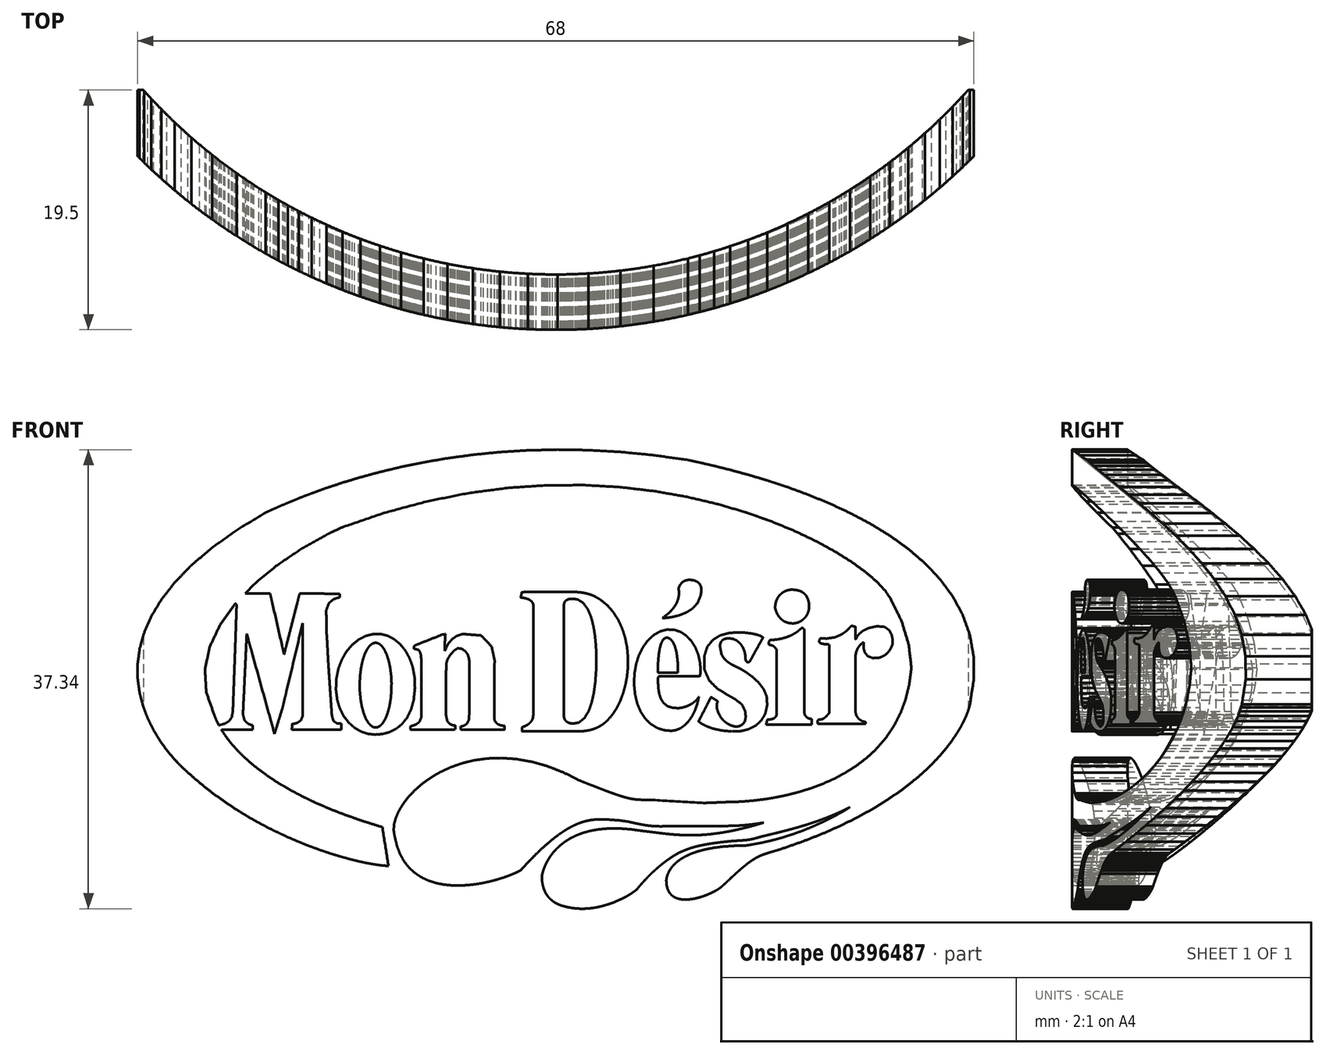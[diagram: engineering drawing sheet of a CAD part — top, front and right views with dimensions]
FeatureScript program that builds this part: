
annotation { "Feature Type Name" : "Feature", "Feature Type Description" : "" }
export const myFeature = defineFeature(function(context is Context, id is Id, definition is map)
    precondition{}
    {
        {
            var Q0;
            Q0=qCreatedBy(makeId("Front.planeOp"),FACE);
            var sketch = newSketch(context, id + "F0", { "sketchPlane" : qUnion([Q0])});
            skLineSegment(sketch, "E0", {"start": v(-8.17, -3.89) * mm, "end": v(-8.17, -4) * mm});
            skLineSegment(sketch, "E1", {"start": v(-7.14, 1.98) * mm, "end": v(-7.35, 2.28) * mm});
            skLineSegment(sketch, "E2", {"start": v(-7.35, 2.28) * mm, "end": v(-7.63, 2.47) * mm});
            skLineSegment(sketch, "E3", {"start": v(-5.22, 2.66) * mm, "end": v(-4.97, 1.53) * mm});
            skLineSegment(sketch, "E4", {"start": v(-6.04, -4.1) * mm, "end": v(-7.2, -4.1) * mm});
            skLineSegment(sketch, "E5", {"start": v(-7.56, 3.68) * mm, "end": v(-6.07, 3.56) * mm});
            skLineSegment(sketch, "E6", {"start": v(-7.63, 2.47) * mm, "end": v(-7.95, 2.52) * mm});
            skLineSegment(sketch, "E7", {"start": v(-8.24, 2.35) * mm, "end": v(-8.55, 2.01) * mm});
            skLineSegment(sketch, "E8", {"start": v(-8.55, 2.01) * mm, "end": v(-8.8, 1.6) * mm});
            skLineSegment(sketch, "E9", {"start": v(-7.95, 2.52) * mm, "end": v(-8.24, 2.35) * mm});
            skLineSegment(sketch, "E10", {"start": v(-8.91, 0.7) * mm, "end": v(-8.92, -0.57) * mm});
            skLineSegment(sketch, "E11", {"start": v(-7.04, 1.63) * mm, "end": v(-7.14, 1.98) * mm});
            skLineSegment(sketch, "E12", {"start": v(-8.93, -2) * mm, "end": v(-8.9, -3.03) * mm});
            skLineSegment(sketch, "E13", {"start": v(-6.07, 3.56) * mm, "end": v(-5.22, 2.66) * mm});
            skLineSegment(sketch, "E14", {"start": v(-4.16, -3.8) * mm, "end": v(-4.16, -3.87) * mm});
            skLineSegment(sketch, "E15", {"start": v(-4.22, -3.8) * mm, "end": v(-4.16, -3.8) * mm});
            skLineSegment(sketch, "E16", {"start": v(-4.16, -4.07) * mm, "end": v(-4.17, -4.1) * mm});
            skLineSegment(sketch, "E17", {"start": v(-7.21, -3.61) * mm, "end": v(-7.05, -3.28) * mm});
            skLineSegment(sketch, "E18", {"start": v(-7.05, -3.28) * mm, "end": v(-7.03, -2.64) * mm});
            skLineSegment(sketch, "E19", {"start": v(-7.03, 1.16) * mm, "end": v(-7.03, 1.43) * mm});
            skLineSegment(sketch, "E20", {"start": v(-4.16, -3.97) * mm, "end": v(-4.16, -4.07) * mm});
            skLineSegment(sketch, "E21", {"start": v(-9.01, 2.3) * mm, "end": v(-8.77, 2.86) * mm});
            skLineSegment(sketch, "E22", {"start": v(-7.03, 0.56) * mm, "end": v(-7.03, 0.81) * mm});
            skLineSegment(sketch, "E23", {"start": v(-7.73, -3.98) * mm, "end": v(-7.74, -3.9) * mm});
            skLineSegment(sketch, "E24", {"start": v(-8.9, -3.03) * mm, "end": v(-8.8, -3.45) * mm});
            skLineSegment(sketch, "E25", {"start": v(-8.8, -3.45) * mm, "end": v(-8.58, -3.67) * mm});
            skLineSegment(sketch, "E26", {"start": v(-4.16, -3.87) * mm, "end": v(-4.16, -3.97) * mm});
            skLineSegment(sketch, "E27", {"start": v(-4.99, -2.85) * mm, "end": v(-4.97, -3.37) * mm});
            skLineSegment(sketch, "E28", {"start": v(-8.58, -3.67) * mm, "end": v(-8.33, -3.75) * mm});
            skLineSegment(sketch, "E29", {"start": v(-8.33, -3.75) * mm, "end": v(-8.18, -3.77) * mm});
            skLineSegment(sketch, "E30", {"start": v(-8.18, -3.77) * mm, "end": v(-8.17, -3.8) * mm});
            skLineSegment(sketch, "E31", {"start": v(-4.76, -3.63) * mm, "end": v(-4.46, -3.76) * mm});
            skLineSegment(sketch, "E32", {"start": v(-8.17, -3.8) * mm, "end": v(-8.17, -3.89) * mm});
            skLineSegment(sketch, "E33", {"start": v(-8.92, -0.57) * mm, "end": v(-8.93, -2) * mm});
            skLineSegment(sketch, "E34", {"start": v(-4.98, -1.75) * mm, "end": v(-4.99, -2.85) * mm});
            skLineSegment(sketch, "E35", {"start": v(-7.46, -3.78) * mm, "end": v(-7.21, -3.61) * mm});
            skLineSegment(sketch, "E36", {"start": v(-8.02, 3.53) * mm, "end": v(-7.56, 3.68) * mm});
            skLineSegment(sketch, "E37", {"start": v(-7.2, -4.1) * mm, "end": v(-7.72, -4.1) * mm});
            skLineSegment(sketch, "E38", {"start": v(-7.72, -4.06) * mm, "end": v(-7.73, -3.98) * mm});
            skLineSegment(sketch, "E39", {"start": v(-7.74, -3.85) * mm, "end": v(-7.67, -3.84) * mm});
            skLineSegment(sketch, "E40", {"start": v(-4.99, -0.48) * mm, "end": v(-4.98, -1.75) * mm});
            skLineSegment(sketch, "E41", {"start": v(-17.58, 6.79) * mm, "end": v(-17.58, 6.69) * mm});
            skLineSegment(sketch, "E42", {"start": v(-8.43, 3.26) * mm, "end": v(-8.02, 3.53) * mm});
            skLineSegment(sketch, "E43", {"start": v(-7.03, -2.64) * mm, "end": v(-7.02, -1.53) * mm});
            skLineSegment(sketch, "E44", {"start": v(-7.03, 0.81) * mm, "end": v(-7.03, 1.16) * mm});
            skLineSegment(sketch, "E45", {"start": v(-7.03, 1.43) * mm, "end": v(-7.04, 1.63) * mm});
            skLineSegment(sketch, "E46", {"start": v(-7.74, -3.9) * mm, "end": v(-7.74, -3.85) * mm});
            skLineSegment(sketch, "E47", {"start": v(-8.8, 1.6) * mm, "end": v(-8.9, 1.25) * mm});
            skLineSegment(sketch, "E48", {"start": v(-7.67, -3.84) * mm, "end": v(-7.46, -3.78) * mm});
            skLineSegment(sketch, "E49", {"start": v(-4.17, -4.1) * mm, "end": v(-4.84, -4.1) * mm});
            skLineSegment(sketch, "E50", {"start": v(-4.46, -3.76) * mm, "end": v(-4.22, -3.8) * mm});
            skLineSegment(sketch, "E51", {"start": v(-4.84, -4.1) * mm, "end": v(-6.04, -4.1) * mm});
            skLineSegment(sketch, "E52", {"start": v(-5, 0.49) * mm, "end": v(-4.99, -0.48) * mm});
            skLineSegment(sketch, "E53", {"start": v(-8.77, 2.86) * mm, "end": v(-8.43, 3.26) * mm});
            skLineSegment(sketch, "E54", {"start": v(-7.72, -4.1) * mm, "end": v(-7.72, -4.06) * mm});
            skLineSegment(sketch, "E55", {"start": v(-7.03, 0.4) * mm, "end": v(-7.03, 0.56) * mm});
            skLineSegment(sketch, "E56", {"start": v(-8.9, 1.25) * mm, "end": v(-8.91, 0.7) * mm});
            skLineSegment(sketch, "E57", {"start": v(-17.58, 6.69) * mm, "end": v(-17.58, 6.64) * mm});
            skLineSegment(sketch, "E58", {"start": v(-4.99, 0.78) * mm, "end": v(-5, 0.49) * mm});
            skLineSegment(sketch, "E59", {"start": v(-4.97, -3.37) * mm, "end": v(-4.76, -3.63) * mm});
            skLineSegment(sketch, "E60", {"start": v(-4.97, 1.53) * mm, "end": v(-4.99, 0.78) * mm});
            skLineSegment(sketch, "E61", {"start": v(-7.02, -1.53) * mm, "end": v(-7.03, -0.38) * mm});
            skLineSegment(sketch, "E62", {"start": v(-7.03, -0.38) * mm, "end": v(-7.03, 0.4) * mm});
            skLineSegment(sketch, "E63", {"start": v(-17.42, -3.85) * mm, "end": v(-17.42, -4.02) * mm});
            skLineSegment(sketch, "E64", {"start": v(-17.42, -4.02) * mm, "end": v(-17.42, -4.1) * mm});
            skLineSegment(sketch, "E65", {"start": v(-18.3, -1.5) * mm, "end": v(-18.2, -2.99) * mm});
            skLineSegment(sketch, "E66", {"start": v(-17.42, -4.1) * mm, "end": v(-18.05, -4.1) * mm});
            skLineSegment(sketch, "E67", {"start": v(-18.05, -4.1) * mm, "end": v(-19.44, -4.1) * mm});
            skLineSegment(sketch, "E68", {"start": v(-18.64, 3.93) * mm, "end": v(-18.49, 1.18) * mm});
            skLineSegment(sketch, "E69", {"start": v(-19.44, -4.1) * mm, "end": v(-20.83, -4.1) * mm});
            skLineSegment(sketch, "E70", {"start": v(-21.43, -3.65) * mm, "end": v(-21.3, -3.63) * mm});
            skLineSegment(sketch, "E71", {"start": v(-20.83, -4.1) * mm, "end": v(-21.46, -4.1) * mm});
            skLineSegment(sketch, "E72", {"start": v(-17.73, 6.62) * mm, "end": v(-18.08, 6.5) * mm});
            skLineSegment(sketch, "E73", {"start": v(-18.49, 1.18) * mm, "end": v(-18.3, -1.5) * mm});
            skLineSegment(sketch, "E74", {"start": v(-17.58, 6.64) * mm, "end": v(-17.73, 6.62) * mm});
            skLineSegment(sketch, "E75", {"start": v(-17.54, -3.61) * mm, "end": v(-17.42, -3.6) * mm});
            skLineSegment(sketch, "E76", {"start": v(-17.42, -3.68) * mm, "end": v(-17.42, -3.85) * mm});
            skLineSegment(sketch, "E77", {"start": v(-21.46, -4.1) * mm, "end": v(-21.46, -4.03) * mm});
            skLineSegment(sketch, "E78", {"start": v(-21.46, -4.03) * mm, "end": v(-21.45, -3.87) * mm});
            skLineSegment(sketch, "E79", {"start": v(-21.44, -3.72) * mm, "end": v(-21.43, -3.65) * mm});
            skLineSegment(sketch, "E80", {"start": v(-21.3, -3.63) * mm, "end": v(-21.02, -3.55) * mm});
            skLineSegment(sketch, "E81", {"start": v(-18.66, 5.6) * mm, "end": v(-18.64, 3.93) * mm});
            skLineSegment(sketch, "E82", {"start": v(-21.02, -3.55) * mm, "end": v(-20.72, -3.35) * mm});
            skLineSegment(sketch, "E83", {"start": v(-18.2, -2.99) * mm, "end": v(-18.06, -3.41) * mm});
            skLineSegment(sketch, "E84", {"start": v(-18.45, 6.19) * mm, "end": v(-18.66, 5.6) * mm});
            skLineSegment(sketch, "E85", {"start": v(-17.42, -3.6) * mm, "end": v(-17.42, -3.68) * mm});
            skLineSegment(sketch, "E86", {"start": v(-20.72, -3.35) * mm, "end": v(-20.58, -2.99) * mm});
            skLineSegment(sketch, "E87", {"start": v(-21.45, -3.87) * mm, "end": v(-21.44, -3.72) * mm});
            skLineSegment(sketch, "E88", {"start": v(-18.06, -3.41) * mm, "end": v(-17.8, -3.59) * mm});
            skLineSegment(sketch, "E89", {"start": v(-20.58, -2.99) * mm, "end": v(-20.57, -1.55) * mm});
            skLineSegment(sketch, "E90", {"start": v(-18.08, 6.5) * mm, "end": v(-18.45, 6.19) * mm});
            skLineSegment(sketch, "E91", {"start": v(-17.8, -3.59) * mm, "end": v(-17.54, -3.61) * mm});
            skLineSegment(sketch, "E92", {"start": v(-27.4, -3.8) * mm, "end": v(-27.4, -3.75) * mm});
            skLineSegment(sketch, "E93", {"start": v(-26.97, -4.1) * mm, "end": v(-27.4, -4.1) * mm});
            skLineSegment(sketch, "E94", {"start": v(-21.96, -1.24) * mm, "end": v(-22.21, -2.31) * mm});
            skLineSegment(sketch, "E95", {"start": v(-22.77, -4.12) * mm, "end": v(-22.87, -4.45) * mm});
            skLineSegment(sketch, "E96", {"start": v(-25.18, 2.67) * mm, "end": v(-25.28, 0.41) * mm});
            skLineSegment(sketch, "E97", {"start": v(-27.4, -4.04) * mm, "end": v(-27.4, -3.93) * mm});
            skLineSegment(sketch, "E98", {"start": v(-24.78, 2.42) * mm, "end": v(-25.13, 3.7) * mm});
            skLineSegment(sketch, "E99", {"start": v(-26.82, 6.61) * mm, "end": v(-26.98, 6.64) * mm});
            skLineSegment(sketch, "E100", {"start": v(-26, 4.46) * mm, "end": v(-25.95, 6.01) * mm});
            skLineSegment(sketch, "E101", {"start": v(-22.27, 2.8) * mm, "end": v(-22.1, 2.01) * mm});
            skLineSegment(sketch, "E102", {"start": v(-23.05, 6.2) * mm, "end": v(-22.66, 4.5) * mm});
            skLineSegment(sketch, "E103", {"start": v(-21.02, 6.2) * mm, "end": v(-20.82, 6.99) * mm});
            skLineSegment(sketch, "E104", {"start": v(-20.82, 6.99) * mm, "end": v(-20.31, 6.98) * mm});
            skLineSegment(sketch, "E105", {"start": v(-21.4, 1.12) * mm, "end": v(-21.96, -1.24) * mm});
            skLineSegment(sketch, "E106", {"start": v(-27.4, -3.93) * mm, "end": v(-27.4, -3.8) * mm});
            skLineSegment(sketch, "E107", {"start": v(-26.98, 6.81) * mm, "end": v(-26.98, 6.93) * mm});
            skLineSegment(sketch, "E108", {"start": v(-26.34, -3.08) * mm, "end": v(-26.26, -2.63) * mm});
            skLineSegment(sketch, "E109", {"start": v(-26.98, 6.93) * mm, "end": v(-26.98, 6.99) * mm});
            skLineSegment(sketch, "E110", {"start": v(-25.13, 3.7) * mm, "end": v(-25.18, 2.67) * mm});
            skLineSegment(sketch, "E111", {"start": v(-26.46, 6.5) * mm, "end": v(-26.82, 6.61) * mm});
            skLineSegment(sketch, "E112", {"start": v(-26.98, 6.99) * mm, "end": v(-26.4, 6.99) * mm});
            skLineSegment(sketch, "E113", {"start": v(-20.83, 3.48) * mm, "end": v(-21.4, 1.12) * mm});
            skLineSegment(sketch, "E114", {"start": v(-26.4, 6.99) * mm, "end": v(-25.1, 6.99) * mm});
            skLineSegment(sketch, "E115", {"start": v(-24, -0.38) * mm, "end": v(-24.78, 2.42) * mm});
            skLineSegment(sketch, "E116", {"start": v(-24.77, -3.73) * mm, "end": v(-24.64, -3.75) * mm});
            skLineSegment(sketch, "E117", {"start": v(-22.54, -3.38) * mm, "end": v(-22.77, -4.12) * mm});
            skLineSegment(sketch, "E118", {"start": v(-26.11, 1.51) * mm, "end": v(-26, 4.46) * mm});
            skLineSegment(sketch, "E119", {"start": v(-20.58, 4.56) * mm, "end": v(-20.83, 3.48) * mm});
            skLineSegment(sketch, "E120", {"start": v(-25.31, -3.34) * mm, "end": v(-25.04, -3.6) * mm});
            skLineSegment(sketch, "E121", {"start": v(-26.55, -3.4) * mm, "end": v(-26.34, -3.08) * mm});
            skLineSegment(sketch, "E122", {"start": v(-26.98, 6.64) * mm, "end": v(-26.98, 6.7) * mm});
            skLineSegment(sketch, "E123", {"start": v(-25.07, -4.1) * mm, "end": v(-26.02, -4.1) * mm});
            skLineSegment(sketch, "E124", {"start": v(-26.98, 6.7) * mm, "end": v(-26.98, 6.81) * mm});
            skLineSegment(sketch, "E125", {"start": v(-27.4, -3.75) * mm, "end": v(-26.9, -3.61) * mm});
            skLineSegment(sketch, "E126", {"start": v(-27.4, -4.1) * mm, "end": v(-27.4, -4.04) * mm});
            skLineSegment(sketch, "E127", {"start": v(-25.28, 0.41) * mm, "end": v(-25.39, -1.84) * mm});
            skLineSegment(sketch, "E128", {"start": v(-22.21, -2.31) * mm, "end": v(-22.32, -2.65) * mm});
            skLineSegment(sketch, "E129", {"start": v(-24.64, -4.1) * mm, "end": v(-25.07, -4.1) * mm});
            skLineSegment(sketch, "E130", {"start": v(-23.82, 6.99) * mm, "end": v(-23.23, 6.99) * mm});
            skLineSegment(sketch, "E131", {"start": v(-23.23, 6.99) * mm, "end": v(-23.05, 6.2) * mm});
            skLineSegment(sketch, "E132", {"start": v(-26.21, -1.35) * mm, "end": v(-26.11, 1.51) * mm});
            skLineSegment(sketch, "E133", {"start": v(-25.04, -3.6) * mm, "end": v(-24.77, -3.73) * mm});
            skLineSegment(sketch, "E134", {"start": v(-20.57, 1.02) * mm, "end": v(-20.57, 3.47) * mm});
            skLineSegment(sketch, "E135", {"start": v(-20.57, -1.55) * mm, "end": v(-20.57, 1.02) * mm});
            skLineSegment(sketch, "E136", {"start": v(-20.57, 3.47) * mm, "end": v(-20.58, 4.56) * mm});
            skLineSegment(sketch, "E137", {"start": v(-22.32, -2.65) * mm, "end": v(-22.54, -3.38) * mm});
            skLineSegment(sketch, "E138", {"start": v(-25.44, -2.86) * mm, "end": v(-25.31, -3.34) * mm});
            skLineSegment(sketch, "E139", {"start": v(-26.02, -4.1) * mm, "end": v(-26.97, -4.1) * mm});
            skLineSegment(sketch, "E140", {"start": v(-26.9, -3.61) * mm, "end": v(-26.55, -3.4) * mm});
            skLineSegment(sketch, "E141", {"start": v(-23.22, -3.18) * mm, "end": v(-24, -0.38) * mm});
            skLineSegment(sketch, "E142", {"start": v(-25.95, 6.01) * mm, "end": v(-26.11, 6.31) * mm});
            skLineSegment(sketch, "E143", {"start": v(-26.11, 6.31) * mm, "end": v(-26.46, 6.5) * mm});
            skLineSegment(sketch, "E144", {"start": v(-26.26, -2.63) * mm, "end": v(-26.21, -1.35) * mm});
            skLineSegment(sketch, "E145", {"start": v(-22.87, -4.45) * mm, "end": v(-23.22, -3.18) * mm});
            skLineSegment(sketch, "E146", {"start": v(-25.39, -1.84) * mm, "end": v(-25.44, -2.86) * mm});
            skLineSegment(sketch, "E147", {"start": v(-22.66, 4.5) * mm, "end": v(-22.27, 2.8) * mm});
            skLineSegment(sketch, "E148", {"start": v(-22.1, 2.01) * mm, "end": v(-21.9, 2.8) * mm});
            skLineSegment(sketch, "E149", {"start": v(-21.9, 2.8) * mm, "end": v(-21.46, 4.5) * mm});
            skLineSegment(sketch, "E150", {"start": v(-25.1, 6.99) * mm, "end": v(-23.82, 6.99) * mm});
            skLineSegment(sketch, "E151", {"start": v(-21.46, 4.5) * mm, "end": v(-21.02, 6.2) * mm});
            skLineSegment(sketch, "E152", {"start": v(-17.58, 6.9) * mm, "end": v(-17.58, 6.79) * mm});
            skLineSegment(sketch, "E153", {"start": v(-20.31, 6.98) * mm, "end": v(-19.2, 6.96) * mm});
            skLineSegment(sketch, "E154", {"start": v(-19.2, 6.96) * mm, "end": v(-18.08, 6.94) * mm});
            skLineSegment(sketch, "E155", {"start": v(-18.08, 6.94) * mm, "end": v(-17.58, 6.94) * mm});
            skLineSegment(sketch, "E156", {"start": v(-17.58, 6.94) * mm, "end": v(-17.58, 6.9) * mm});
            skLineSegment(sketch, "E157", {"start": v(7.1, 2.62) * mm, "end": v(7.51, 3.17) * mm});
            skLineSegment(sketch, "E158", {"start": v(1.44, -3.62) * mm, "end": v(1.89, -3.52) * mm});
            skLineSegment(sketch, "E159", {"start": v(11.32, -2.57) * mm, "end": v(11.08, -3.04) * mm});
            skLineSegment(sketch, "E160", {"start": v(9.79, -4.14) * mm, "end": v(9.41, -4.2) * mm});
            skLineSegment(sketch, "E161", {"start": v(0.66, 2.96) * mm, "end": v(0.66, 1.33) * mm});
            skLineSegment(sketch, "E162", {"start": v(6.4, 0.45) * mm, "end": v(6.54, 1.25) * mm});
            skLineSegment(sketch, "E163", {"start": v(7.51, 3.17) * mm, "end": v(7.98, 3.6) * mm});
            skLineSegment(sketch, "E164", {"start": v(6.46, -1.26) * mm, "end": v(6.37, -0.41) * mm});
            skLineSegment(sketch, "E165", {"start": v(0.68, 6.18) * mm, "end": v(0.66, 6.01) * mm});
            skLineSegment(sketch, "E166", {"start": v(3.1, -1.07) * mm, "end": v(3.22, -0.22) * mm});
            skLineSegment(sketch, "E167", {"start": v(3.27, 2.77) * mm, "end": v(3.19, 3.56) * mm});
            skLineSegment(sketch, "E168", {"start": v(7.98, 3.6) * mm, "end": v(8.5, 3.9) * mm});
            skLineSegment(sketch, "E169", {"start": v(8.5, 3.9) * mm, "end": v(9.07, 4.04) * mm});
            skLineSegment(sketch, "E170", {"start": v(0.66, -1.68) * mm, "end": v(0.66, -2.67) * mm});
            skLineSegment(sketch, "E171", {"start": v(1.26, -3.6) * mm, "end": v(1.36, -3.61) * mm});
            skLineSegment(sketch, "E172", {"start": v(11.5, -2.03) * mm, "end": v(11.32, -2.57) * mm});
            skLineSegment(sketch, "E173", {"start": v(7.73, -3.65) * mm, "end": v(7.29, -3.22) * mm});
            skLineSegment(sketch, "E174", {"start": v(1.1, 6.52) * mm, "end": v(0.97, 6.48) * mm});
            skLineSegment(sketch, "E175", {"start": v(0.66, -2.67) * mm, "end": v(0.66, -3.04) * mm});
            skLineSegment(sketch, "E176", {"start": v(3.22, -0.22) * mm, "end": v(3.28, 0.61) * mm});
            skLineSegment(sketch, "E177", {"start": v(3.3, 2.03) * mm, "end": v(3.27, 2.77) * mm});
            skLineSegment(sketch, "E178", {"start": v(0.7, -3.22) * mm, "end": v(0.79, -3.36) * mm});
            skLineSegment(sketch, "E179", {"start": v(1.02, -3.53) * mm, "end": v(1.14, -3.57) * mm});
            skLineSegment(sketch, "E180", {"start": v(3.06, 4.35) * mm, "end": v(2.86, 5.09) * mm});
            skLineSegment(sketch, "E181", {"start": v(1.77, 6.49) * mm, "end": v(1.42, 6.54) * mm});
            skLineSegment(sketch, "E182", {"start": v(1.34, 6.54) * mm, "end": v(1.23, 6.54) * mm});
            skLineSegment(sketch, "E183", {"start": v(0.66, 4.42) * mm, "end": v(0.66, 2.96) * mm});
            skLineSegment(sketch, "E184", {"start": v(0.66, -0.29) * mm, "end": v(0.66, -1.68) * mm});
            skLineSegment(sketch, "E185", {"start": v(10.8, -3.43) * mm, "end": v(10.49, -3.75) * mm});
            skLineSegment(sketch, "E186", {"start": v(8.82, -4.15) * mm, "end": v(8.25, -3.97) * mm});
            skLineSegment(sketch, "E187", {"start": v(1.89, -3.52) * mm, "end": v(2.33, -3.17) * mm});
            skLineSegment(sketch, "E188", {"start": v(7.29, -3.22) * mm, "end": v(6.92, -2.67) * mm});
            skLineSegment(sketch, "E189", {"start": v(6.92, -2.67) * mm, "end": v(6.64, -2.02) * mm});
            skLineSegment(sketch, "E190", {"start": v(3.19, 3.56) * mm, "end": v(3.06, 4.35) * mm});
            skLineSegment(sketch, "E191", {"start": v(0.79, -3.36) * mm, "end": v(0.9, -3.46) * mm});
            skLineSegment(sketch, "E192", {"start": v(0.97, 6.48) * mm, "end": v(0.85, 6.42) * mm});
            skLineSegment(sketch, "E193", {"start": v(0.9, -3.46) * mm, "end": v(1.02, -3.53) * mm});
            skLineSegment(sketch, "E194", {"start": v(3.3, 1.37) * mm, "end": v(3.3, 2.03) * mm});
            skLineSegment(sketch, "E195", {"start": v(0.85, 6.42) * mm, "end": v(0.75, 6.32) * mm});
            skLineSegment(sketch, "E196", {"start": v(0.66, 1.33) * mm, "end": v(0.66, -0.29) * mm});
            skLineSegment(sketch, "E197", {"start": v(1.14, -3.57) * mm, "end": v(1.26, -3.6) * mm});
            skLineSegment(sketch, "E198", {"start": v(2.23, 6.2) * mm, "end": v(1.77, 6.49) * mm});
            skLineSegment(sketch, "E199", {"start": v(11.64, -1.44) * mm, "end": v(11.5, -2.03) * mm});
            skLineSegment(sketch, "E200", {"start": v(9.41, -4.2) * mm, "end": v(8.82, -4.15) * mm});
            skLineSegment(sketch, "E201", {"start": v(8.25, -3.97) * mm, "end": v(7.73, -3.65) * mm});
            skLineSegment(sketch, "E202", {"start": v(10.49, -3.75) * mm, "end": v(10.15, -4) * mm});
            skLineSegment(sketch, "E203", {"start": v(1.23, 6.54) * mm, "end": v(1.1, 6.52) * mm});
            skLineSegment(sketch, "E204", {"start": v(10.15, -4) * mm, "end": v(9.79, -4.14) * mm});
            skLineSegment(sketch, "E205", {"start": v(0.66, 6.01) * mm, "end": v(0.66, 5.5) * mm});
            skLineSegment(sketch, "E206", {"start": v(2.6, 5.73) * mm, "end": v(2.23, 6.2) * mm});
            skLineSegment(sketch, "E207", {"start": v(1.36, -3.61) * mm, "end": v(1.44, -3.62) * mm});
            skLineSegment(sketch, "E208", {"start": v(6.64, -2.02) * mm, "end": v(6.46, -1.26) * mm});
            skLineSegment(sketch, "E209", {"start": v(2.33, -3.17) * mm, "end": v(2.68, -2.6) * mm});
            skLineSegment(sketch, "E210", {"start": v(1.42, 6.54) * mm, "end": v(1.34, 6.54) * mm});
            skLineSegment(sketch, "E211", {"start": v(0.66, 5.5) * mm, "end": v(0.66, 4.42) * mm});
            skLineSegment(sketch, "E212", {"start": v(2.93, -1.88) * mm, "end": v(3.1, -1.07) * mm});
            skLineSegment(sketch, "E213", {"start": v(6.37, -0.41) * mm, "end": v(6.4, 0.45) * mm});
            skLineSegment(sketch, "E214", {"start": v(0.75, 6.32) * mm, "end": v(0.68, 6.18) * mm});
            skLineSegment(sketch, "E215", {"start": v(6.54, 1.25) * mm, "end": v(6.78, 1.98) * mm});
            skLineSegment(sketch, "E216", {"start": v(6.78, 1.98) * mm, "end": v(7.1, 2.62) * mm});
            skLineSegment(sketch, "E217", {"start": v(2.68, -2.6) * mm, "end": v(2.93, -1.88) * mm});
            skLineSegment(sketch, "E218", {"start": v(3.28, 0.61) * mm, "end": v(3.3, 1.37) * mm});
            skLineSegment(sketch, "E219", {"start": v(2.86, 5.09) * mm, "end": v(2.6, 5.73) * mm});
            skLineSegment(sketch, "E220", {"start": v(11.08, -3.04) * mm, "end": v(10.8, -3.43) * mm});
            skLineSegment(sketch, "E221", {"start": v(11.52, -1.61) * mm, "end": v(11.64, -1.44) * mm});
            skLineSegment(sketch, "E222", {"start": v(9.94, 0.53) * mm, "end": v(9.91, 1.48) * mm});
            skLineSegment(sketch, "E223", {"start": v(12.33, -2.04) * mm, "end": v(12.53, -1.66) * mm});
            skLineSegment(sketch, "E224", {"start": v(8.32, 0.1) * mm, "end": v(8.32, -0.29) * mm});
            skLineSegment(sketch, "E225", {"start": v(12.53, -1.66) * mm, "end": v(12.63, -1.46) * mm});
            skLineSegment(sketch, "E226", {"start": v(8.34, 1.6) * mm, "end": v(8.31, 1.15) * mm});
            skLineSegment(sketch, "E227", {"start": v(8.35, -0.72) * mm, "end": v(8.4, -1.15) * mm});
            skLineSegment(sketch, "E228", {"start": v(11.78, 0.6) * mm, "end": v(11.72, 0.23) * mm});
            skLineSegment(sketch, "E229", {"start": v(11.6, 2) * mm, "end": v(11.74, 1.32) * mm});
            skLineSegment(sketch, "E230", {"start": v(9.36, 3.24) * mm, "end": v(9.2, 3.34) * mm});
            skLineSegment(sketch, "E231", {"start": v(10.7, -2.18) * mm, "end": v(10.93, -2.08) * mm});
            skLineSegment(sketch, "E232", {"start": v(9.08, 3.38) * mm, "end": v(9.02, 3.38) * mm});
            skLineSegment(sketch, "E233", {"start": v(10.47, -2.26) * mm, "end": v(10.7, -2.18) * mm});
            skLineSegment(sketch, "E234", {"start": v(8.4, -1.15) * mm, "end": v(8.54, -1.56) * mm});
            skLineSegment(sketch, "E235", {"start": v(8.54, -1.56) * mm, "end": v(8.75, -1.92) * mm});
            skLineSegment(sketch, "E236", {"start": v(8.7, 3.16) * mm, "end": v(8.56, 2.87) * mm});
            skLineSegment(sketch, "E237", {"start": v(9.69, 2.7) * mm, "end": v(9.52, 3.03) * mm});
            skLineSegment(sketch, "E238", {"start": v(8.56, 2.87) * mm, "end": v(8.46, 2.49) * mm});
            skLineSegment(sketch, "E239", {"start": v(10.03, -2.35) * mm, "end": v(10.24, -2.32) * mm});
            skLineSegment(sketch, "E240", {"start": v(9.07, 4.04) * mm, "end": v(9.63, 4.02) * mm});
            skLineSegment(sketch, "E241", {"start": v(11.15, -1.94) * mm, "end": v(11.35, -1.79) * mm});
            skLineSegment(sketch, "E242", {"start": v(9.82, 2.19) * mm, "end": v(9.69, 2.7) * mm});
            skLineSegment(sketch, "E243", {"start": v(8.75, -1.92) * mm, "end": v(9.08, -2.19) * mm});
            skLineSegment(sketch, "E244", {"start": v(8.38, 0.23) * mm, "end": v(8.32, 0.1) * mm});
            skLineSegment(sketch, "E245", {"start": v(11.02, 3.12) * mm, "end": v(11.35, 2.6) * mm});
            skLineSegment(sketch, "E246", {"start": v(9.54, -2.34) * mm, "end": v(10.03, -2.35) * mm});
            skLineSegment(sketch, "E247", {"start": v(8.46, 2.49) * mm, "end": v(8.39, 2.05) * mm});
            skLineSegment(sketch, "E248", {"start": v(11.35, -1.79) * mm, "end": v(11.52, -1.61) * mm});
            skLineSegment(sketch, "E249", {"start": v(9.91, 1.48) * mm, "end": v(9.82, 2.19) * mm});
            skLineSegment(sketch, "E250", {"start": v(8.39, 2.05) * mm, "end": v(8.34, 1.6) * mm});
            skLineSegment(sketch, "E251", {"start": v(8.31, 1.15) * mm, "end": v(8.3, 0.76) * mm});
            skLineSegment(sketch, "E252", {"start": v(10.93, -2.08) * mm, "end": v(11.15, -1.94) * mm});
            skLineSegment(sketch, "E253", {"start": v(9.52, 3.03) * mm, "end": v(9.36, 3.24) * mm});
            skLineSegment(sketch, "E254", {"start": v(8.3, 0.53) * mm, "end": v(8.41, 0.53) * mm});
            skLineSegment(sketch, "E255", {"start": v(10.24, -2.32) * mm, "end": v(10.47, -2.26) * mm});
            skLineSegment(sketch, "E256", {"start": v(11.86, -2.96) * mm, "end": v(12.1, -2.5) * mm});
            skLineSegment(sketch, "E257", {"start": v(12.1, -2.5) * mm, "end": v(12.33, -2.04) * mm});
            skLineSegment(sketch, "E258", {"start": v(10.62, 3.54) * mm, "end": v(11.02, 3.12) * mm});
            skLineSegment(sketch, "E259", {"start": v(11.69, -3.3) * mm, "end": v(11.86, -2.96) * mm});
            skLineSegment(sketch, "E260", {"start": v(9.63, 4.02) * mm, "end": v(10.15, 3.85) * mm});
            skLineSegment(sketch, "E261", {"start": v(9.2, 3.34) * mm, "end": v(9.08, 3.38) * mm});
            skLineSegment(sketch, "E262", {"start": v(11.74, 1.32) * mm, "end": v(11.78, 0.6) * mm});
            skLineSegment(sketch, "E263", {"start": v(8.87, 3.34) * mm, "end": v(8.7, 3.16) * mm});
            skLineSegment(sketch, "E264", {"start": v(11.35, 2.6) * mm, "end": v(11.6, 2) * mm});
            skLineSegment(sketch, "E265", {"start": v(10.15, 3.85) * mm, "end": v(10.62, 3.54) * mm});
            skLineSegment(sketch, "E266", {"start": v(8.32, -0.29) * mm, "end": v(8.35, -0.72) * mm});
            skLineSegment(sketch, "E267", {"start": v(8.3, 0.76) * mm, "end": v(8.3, 0.53) * mm});
            skLineSegment(sketch, "E268", {"start": v(9.02, 3.38) * mm, "end": v(8.87, 3.34) * mm});
            skLineSegment(sketch, "E269", {"start": v(9.08, -2.19) * mm, "end": v(9.54, -2.34) * mm});
            skLineSegment(sketch, "E270", {"start": v(11.62, -3.44) * mm, "end": v(11.69, -3.3) * mm});
            skLineSegment(sketch, "E271", {"start": v(15.95, 3.71) * mm, "end": v(16.34, 3.63) * mm});
            skLineSegment(sketch, "E272", {"start": v(16.6, 3.54) * mm, "end": v(16.76, 3.46) * mm});
            skLineSegment(sketch, "E273", {"start": v(14.74, 3.13) * mm, "end": v(14.38, 3.3) * mm});
            skLineSegment(sketch, "E274", {"start": v(14.38, 3.3) * mm, "end": v(13.95, 3.33) * mm});
            skLineSegment(sketch, "E275", {"start": v(13.18, -1.8) * mm, "end": v(13.16, -1.87) * mm});
            skLineSegment(sketch, "E276", {"start": v(15.64, 1.38) * mm, "end": v(15.56, 1.38) * mm});
            skLineSegment(sketch, "E277", {"start": v(13.62, 3.23) * mm, "end": v(13.44, 3.05) * mm});
            skLineSegment(sketch, "E278", {"start": v(14.65, -3.86) * mm, "end": v(14.81, -3.85) * mm});
            skLineSegment(sketch, "E279", {"start": v(13.12, -1.98) * mm, "end": v(13.1, -2.16) * mm});
            skLineSegment(sketch, "E280", {"start": v(14.75, 3.8) * mm, "end": v(15.4, 3.78) * mm});
            skLineSegment(sketch, "E281", {"start": v(13.86, -1.22) * mm, "end": v(13.12, -0.74) * mm});
            skLineSegment(sketch, "E282", {"start": v(15.4, 3.78) * mm, "end": v(15.95, 3.71) * mm});
            skLineSegment(sketch, "E283", {"start": v(16.36, 2.48) * mm, "end": v(16.1, 2.02) * mm});
            skLineSegment(sketch, "E284", {"start": v(13.95, 3.33) * mm, "end": v(13.62, 3.23) * mm});
            skLineSegment(sketch, "E285", {"start": v(12.66, -1.47) * mm, "end": v(12.74, -1.52) * mm});
            skLineSegment(sketch, "E286", {"start": v(15.22, -3.66) * mm, "end": v(15.38, -3.43) * mm});
            skLineSegment(sketch, "E287", {"start": v(16.34, 3.63) * mm, "end": v(16.6, 3.54) * mm});
            skLineSegment(sketch, "E288", {"start": v(15.8, 1.46) * mm, "end": v(15.78, 1.44) * mm});
            skLineSegment(sketch, "E289", {"start": v(15.72, 1.4) * mm, "end": v(15.64, 1.38) * mm});
            skLineSegment(sketch, "E290", {"start": v(13, -1.68) * mm, "end": v(13.11, -1.76) * mm});
            skLineSegment(sketch, "E291", {"start": v(15.02, 2.88) * mm, "end": v(14.74, 3.13) * mm});
            skLineSegment(sketch, "E292", {"start": v(13.93, -3.6) * mm, "end": v(14.2, -3.74) * mm});
            skLineSegment(sketch, "E293", {"start": v(13.12, -0.74) * mm, "end": v(12.48, -0.1) * mm});
            skLineSegment(sketch, "E294", {"start": v(12.63, -1.46) * mm, "end": v(12.66, -1.47) * mm});
            skLineSegment(sketch, "E295", {"start": v(14.43, -3.82) * mm, "end": v(14.59, -3.85) * mm});
            skLineSegment(sketch, "E296", {"start": v(13.16, -1.87) * mm, "end": v(13.12, -1.98) * mm});
            skLineSegment(sketch, "E297", {"start": v(15.02, -3.79) * mm, "end": v(15.22, -3.66) * mm});
            skLineSegment(sketch, "E298", {"start": v(12.86, -1.6) * mm, "end": v(13, -1.68) * mm});
            skLineSegment(sketch, "E299", {"start": v(13.66, -3.38) * mm, "end": v(13.93, -3.6) * mm});
            skLineSegment(sketch, "E300", {"start": v(15.14, -2.05) * mm, "end": v(14.58, -1.63) * mm});
            skLineSegment(sketch, "E301", {"start": v(14.59, -3.85) * mm, "end": v(14.65, -3.86) * mm});
            skLineSegment(sketch, "E302", {"start": v(12.48, -0.1) * mm, "end": v(12.1, 0.78) * mm});
            skLineSegment(sketch, "E303", {"start": v(12.79, 3.2) * mm, "end": v(13.38, 3.56) * mm});
            skLineSegment(sketch, "E304", {"start": v(16.84, 3.4) * mm, "end": v(16.86, 3.38) * mm});
            skLineSegment(sketch, "E305", {"start": v(16.76, 3.46) * mm, "end": v(16.84, 3.4) * mm});
            skLineSegment(sketch, "E306", {"start": v(16.79, 3.25) * mm, "end": v(16.6, 2.92) * mm});
            skLineSegment(sketch, "E307", {"start": v(16.6, 2.92) * mm, "end": v(16.36, 2.48) * mm});
            skLineSegment(sketch, "E308", {"start": v(13.4, -3.07) * mm, "end": v(13.66, -3.38) * mm});
            skLineSegment(sketch, "E309", {"start": v(14.58, -1.63) * mm, "end": v(13.86, -1.22) * mm});
            skLineSegment(sketch, "E310", {"start": v(12.74, -1.52) * mm, "end": v(12.86, -1.6) * mm});
            skLineSegment(sketch, "E311", {"start": v(15.9, 1.65) * mm, "end": v(15.8, 1.46) * mm});
            skLineSegment(sketch, "E312", {"start": v(13.1, -2.16) * mm, "end": v(13.12, -2.4) * mm});
            skLineSegment(sketch, "E313", {"start": v(15.56, 1.38) * mm, "end": v(15.48, 1.46) * mm});
            skLineSegment(sketch, "E314", {"start": v(15.44, 1.63) * mm, "end": v(15.43, 1.9) * mm});
            skLineSegment(sketch, "E315", {"start": v(15.43, 1.9) * mm, "end": v(15.36, 2.24) * mm});
            skLineSegment(sketch, "E316", {"start": v(13.12, -2.4) * mm, "end": v(13.21, -2.7) * mm});
            skLineSegment(sketch, "E317", {"start": v(13.21, -2.7) * mm, "end": v(13.4, -3.07) * mm});
            skLineSegment(sketch, "E318", {"start": v(15.36, 2.24) * mm, "end": v(15.23, 2.57) * mm});
            skLineSegment(sketch, "E319", {"start": v(12.33, 2.65) * mm, "end": v(12.79, 3.2) * mm});
            skLineSegment(sketch, "E320", {"start": v(15.38, -3.43) * mm, "end": v(15.46, -3.08) * mm});
            skLineSegment(sketch, "E321", {"start": v(13.11, -1.76) * mm, "end": v(13.18, -1.8) * mm});
            skLineSegment(sketch, "E322", {"start": v(12.1, 0.78) * mm, "end": v(12.08, 1.85) * mm});
            skLineSegment(sketch, "E323", {"start": v(15.78, 1.44) * mm, "end": v(15.72, 1.4) * mm});
            skLineSegment(sketch, "E324", {"start": v(14.2, -3.74) * mm, "end": v(14.43, -3.82) * mm});
            skLineSegment(sketch, "E325", {"start": v(16.86, 3.38) * mm, "end": v(16.79, 3.25) * mm});
            skLineSegment(sketch, "E326", {"start": v(15.48, 1.46) * mm, "end": v(15.44, 1.63) * mm});
            skLineSegment(sketch, "E327", {"start": v(12.08, 1.85) * mm, "end": v(12.33, 2.65) * mm});
            skLineSegment(sketch, "E328", {"start": v(14.81, -3.85) * mm, "end": v(15.02, -3.79) * mm});
            skLineSegment(sketch, "E329", {"start": v(13.38, 3.56) * mm, "end": v(14.05, 3.75) * mm});
            skLineSegment(sketch, "E330", {"start": v(15.4, -2.57) * mm, "end": v(15.14, -2.05) * mm});
            skLineSegment(sketch, "E331", {"start": v(14.05, 3.75) * mm, "end": v(14.75, 3.8) * mm});
            skLineSegment(sketch, "E332", {"start": v(16.1, 2.02) * mm, "end": v(15.9, 1.65) * mm});
            skLineSegment(sketch, "E333", {"start": v(15.46, -3.08) * mm, "end": v(15.4, -2.57) * mm});
            skLineSegment(sketch, "E334", {"start": v(15.23, 2.57) * mm, "end": v(15.02, 2.88) * mm});
            skLineSegment(sketch, "E335", {"start": v(20.38, 6.78) * mm, "end": v(20.5, 6.54) * mm});
            skLineSegment(sketch, "E336", {"start": v(14.38, 1.15) * mm, "end": v(14.6, 1.05) * mm});
            skLineSegment(sketch, "E337", {"start": v(13.87, 1.5) * mm, "end": v(14.13, 1.3) * mm});
            skLineSegment(sketch, "E338", {"start": v(13.4, 2.44) * mm, "end": v(13.42, 2.37) * mm});
            skLineSegment(sketch, "E339", {"start": v(13.64, 1.75) * mm, "end": v(13.87, 1.5) * mm});
            skLineSegment(sketch, "E340", {"start": v(16.5, -0.27) * mm, "end": v(16.9, -0.8) * mm});
            skLineSegment(sketch, "E341", {"start": v(11.9, -3.64) * mm, "end": v(11.68, -3.5) * mm});
            skLineSegment(sketch, "E342", {"start": v(20.48, 5.3) * mm, "end": v(20.34, 5.08) * mm});
            skLineSegment(sketch, "E343", {"start": v(20.16, 4.89) * mm, "end": v(19.95, 4.73) * mm});
            skLineSegment(sketch, "E344", {"start": v(17.04, -2.83) * mm, "end": v(16.7, -3.39) * mm});
            skLineSegment(sketch, "E345", {"start": v(19.95, 4.73) * mm, "end": v(19.73, 4.62) * mm});
            skLineSegment(sketch, "E346", {"start": v(20.34, 5.08) * mm, "end": v(20.16, 4.89) * mm});
            skLineSegment(sketch, "E347", {"start": v(19.73, 4.62) * mm, "end": v(19.5, 4.56) * mm});
            skLineSegment(sketch, "E348", {"start": v(19.8, 7.2) * mm, "end": v(20.02, 7.1) * mm});
            skLineSegment(sketch, "E349", {"start": v(16.9, -0.8) * mm, "end": v(17.15, -1.38) * mm});
            skLineSegment(sketch, "E350", {"start": v(18.2, 6.83) * mm, "end": v(18.4, 7) * mm});
            skLineSegment(sketch, "E351", {"start": v(20.57, 5.57) * mm, "end": v(20.48, 5.3) * mm});
            skLineSegment(sketch, "E352", {"start": v(19.5, 4.56) * mm, "end": v(19.27, 4.53) * mm});
            skLineSegment(sketch, "E353", {"start": v(17.2, -2.1) * mm, "end": v(17.04, -2.83) * mm});
            skLineSegment(sketch, "E354", {"start": v(19.08, 7.27) * mm, "end": v(19.32, 7.28) * mm});
            skLineSegment(sketch, "E355", {"start": v(18.3, 4.91) * mm, "end": v(18.12, 5.13) * mm});
            skLineSegment(sketch, "E356", {"start": v(16, 0.2) * mm, "end": v(16.5, -0.27) * mm});
            skLineSegment(sketch, "E357", {"start": v(16.7, -3.39) * mm, "end": v(16.23, -3.8) * mm});
            skLineSegment(sketch, "E358", {"start": v(14.34, -4.25) * mm, "end": v(13.47, -4.17) * mm});
            skLineSegment(sketch, "E359", {"start": v(19.27, 4.53) * mm, "end": v(18.87, 4.58) * mm});
            skLineSegment(sketch, "E360", {"start": v(18.05, 6.61) * mm, "end": v(18.2, 6.83) * mm});
            skLineSegment(sketch, "E361", {"start": v(19.56, 7.25) * mm, "end": v(19.8, 7.2) * mm});
            skLineSegment(sketch, "E362", {"start": v(13.37, 2.6) * mm, "end": v(13.4, 2.44) * mm});
            skLineSegment(sketch, "E363", {"start": v(14.6, 1.05) * mm, "end": v(14.96, 0.87) * mm});
            skLineSegment(sketch, "E364", {"start": v(12.25, -3.82) * mm, "end": v(11.9, -3.64) * mm});
            skLineSegment(sketch, "E365", {"start": v(18.55, 4.72) * mm, "end": v(18.3, 4.91) * mm});
            skLineSegment(sketch, "E366", {"start": v(17.93, 6.36) * mm, "end": v(18.05, 6.61) * mm});
            skLineSegment(sketch, "E367", {"start": v(19.32, 7.28) * mm, "end": v(19.56, 7.25) * mm});
            skLineSegment(sketch, "E368", {"start": v(20.58, 6.23) * mm, "end": v(20.61, 5.87) * mm});
            skLineSegment(sketch, "E369", {"start": v(8.66, 4.96) * mm, "end": v(8.78, 4.97) * mm});
            skLineSegment(sketch, "E370", {"start": v(8.78, 4.97) * mm, "end": v(9.1, 5) * mm});
            skLineSegment(sketch, "E371", {"start": v(12.78, -4.02) * mm, "end": v(12.25, -3.82) * mm});
            skLineSegment(sketch, "E372", {"start": v(17.84, 5.81) * mm, "end": v(17.86, 6.07) * mm});
            skLineSegment(sketch, "E373", {"start": v(18.87, 4.58) * mm, "end": v(18.55, 4.72) * mm});
            skLineSegment(sketch, "E374", {"start": v(13.44, 3.05) * mm, "end": v(13.37, 2.82) * mm});
            skLineSegment(sketch, "E375", {"start": v(15.46, 0.58) * mm, "end": v(16, 0.2) * mm});
            skLineSegment(sketch, "E376", {"start": v(18.4, 7) * mm, "end": v(18.6, 7.14) * mm});
            skLineSegment(sketch, "E377", {"start": v(17.15, -1.38) * mm, "end": v(17.2, -2.1) * mm});
            skLineSegment(sketch, "E378", {"start": v(15.66, -4.08) * mm, "end": v(15.05, -4.22) * mm});
            skLineSegment(sketch, "E379", {"start": v(20.02, 7.1) * mm, "end": v(20.21, 6.97) * mm});
            skLineSegment(sketch, "E380", {"start": v(17.99, 5.36) * mm, "end": v(17.9, 5.57) * mm});
            skLineSegment(sketch, "E381", {"start": v(13.37, 2.82) * mm, "end": v(13.37, 2.6) * mm});
            skLineSegment(sketch, "E382", {"start": v(14.96, 0.87) * mm, "end": v(15.46, 0.58) * mm});
            skLineSegment(sketch, "E383", {"start": v(18.12, 5.13) * mm, "end": v(17.99, 5.36) * mm});
            skLineSegment(sketch, "E384", {"start": v(17.86, 5.73) * mm, "end": v(17.84, 5.81) * mm});
            skLineSegment(sketch, "E385", {"start": v(18.6, 7.14) * mm, "end": v(18.84, 7.23) * mm});
            skLineSegment(sketch, "E386", {"start": v(16.23, -3.8) * mm, "end": v(15.66, -4.08) * mm});
            skLineSegment(sketch, "E387", {"start": v(13.48, 2.04) * mm, "end": v(13.64, 1.75) * mm});
            skLineSegment(sketch, "E388", {"start": v(15.05, -4.22) * mm, "end": v(14.34, -4.25) * mm});
            skLineSegment(sketch, "E389", {"start": v(18.84, 7.23) * mm, "end": v(19.08, 7.27) * mm});
            skLineSegment(sketch, "E390", {"start": v(20.5, 6.54) * mm, "end": v(20.58, 6.23) * mm});
            skLineSegment(sketch, "E391", {"start": v(13.42, 2.37) * mm, "end": v(13.48, 2.04) * mm});
            skLineSegment(sketch, "E392", {"start": v(17.9, 5.57) * mm, "end": v(17.86, 5.73) * mm});
            skLineSegment(sketch, "E393", {"start": v(20.61, 5.87) * mm, "end": v(20.57, 5.57) * mm});
            skLineSegment(sketch, "E394", {"start": v(14.13, 1.3) * mm, "end": v(14.38, 1.15) * mm});
            skLineSegment(sketch, "E395", {"start": v(11.68, -3.5) * mm, "end": v(11.62, -3.44) * mm});
            skLineSegment(sketch, "E396", {"start": v(20.21, 6.97) * mm, "end": v(20.38, 6.78) * mm});
            skLineSegment(sketch, "E397", {"start": v(13.47, -4.17) * mm, "end": v(12.78, -4.02) * mm});
            skLineSegment(sketch, "E398", {"start": v(17.86, 6.07) * mm, "end": v(17.93, 6.36) * mm});
            skLineSegment(sketch, "E399", {"start": v(11.84, 7.4) * mm, "end": v(11.8, 7.59) * mm});
            skLineSegment(sketch, "E400", {"start": v(10.27, 7.86) * mm, "end": v(10.14, 7.71) * mm});
            skLineSegment(sketch, "E401", {"start": v(20.2, 4.05) * mm, "end": v(20.22, 3.78) * mm});
            skLineSegment(sketch, "E402", {"start": v(20.23, -2.79) * mm, "end": v(20.26, -2.89) * mm});
            skLineSegment(sketch, "E403", {"start": v(18, 3.23) * mm, "end": v(18.38, 3.3) * mm});
            skLineSegment(sketch, "E404", {"start": v(10, 7.37) * mm, "end": v(10, 7.27) * mm});
            skLineSegment(sketch, "E405", {"start": v(20.26, -2.89) * mm, "end": v(20.32, -3) * mm});
            skLineSegment(sketch, "E406", {"start": v(10.06, 7.57) * mm, "end": v(10.01, 7.45) * mm});
            skLineSegment(sketch, "E407", {"start": v(10.02, 6.85) * mm, "end": v(9.96, 6.54) * mm});
            skLineSegment(sketch, "E408", {"start": v(20.32, -3) * mm, "end": v(20.4, -3.1) * mm});
            skLineSegment(sketch, "E409", {"start": v(9.83, 6.18) * mm, "end": v(9.58, 5.78) * mm});
            skLineSegment(sketch, "E410", {"start": v(11.85, 7.24) * mm, "end": v(11.84, 7.4) * mm});
            skLineSegment(sketch, "E411", {"start": v(17.5, 3.18) * mm, "end": v(17.7, 3.2) * mm});
            skLineSegment(sketch, "E412", {"start": v(20.2, 4.07) * mm, "end": v(20.2, 4.05) * mm});
            skLineSegment(sketch, "E413", {"start": v(11.8, 7.59) * mm, "end": v(11.7, 7.76) * mm});
            skLineSegment(sketch, "E414", {"start": v(10.66, 8.06) * mm, "end": v(10.43, 7.98) * mm});
            skLineSegment(sketch, "E415", {"start": v(9.96, 6.54) * mm, "end": v(9.83, 6.18) * mm});
            skLineSegment(sketch, "E416", {"start": v(17.7, 3.2) * mm, "end": v(18, 3.23) * mm});
            skLineSegment(sketch, "E417", {"start": v(19.98, 4.14) * mm, "end": v(20.02, 4.16) * mm});
            skLineSegment(sketch, "E418", {"start": v(11.16, 5.77) * mm, "end": v(11.56, 6.22) * mm});
            skLineSegment(sketch, "E419", {"start": v(10.65, 5.44) * mm, "end": v(11.16, 5.77) * mm});
            skLineSegment(sketch, "E420", {"start": v(11.52, 7.92) * mm, "end": v(11.27, 8.03) * mm});
            skLineSegment(sketch, "E421", {"start": v(9.58, 5.78) * mm, "end": v(9.2, 5.37) * mm});
            skLineSegment(sketch, "E422", {"start": v(20.1, 4.16) * mm, "end": v(20.13, 4.13) * mm});
            skLineSegment(sketch, "E423", {"start": v(19.94, 4.1) * mm, "end": v(19.98, 4.14) * mm});
            skLineSegment(sketch, "E424", {"start": v(10, 7.27) * mm, "end": v(10.03, 7.1) * mm});
            skLineSegment(sketch, "E425", {"start": v(20.16, 4.1) * mm, "end": v(20.2, 4.07) * mm});
            skLineSegment(sketch, "E426", {"start": v(20.22, 0.59) * mm, "end": v(20.22, -0.69) * mm});
            skLineSegment(sketch, "E427", {"start": v(10.43, 7.98) * mm, "end": v(10.27, 7.86) * mm});
            skLineSegment(sketch, "E428", {"start": v(20.22, -1.77) * mm, "end": v(20.22, -2.48) * mm});
            skLineSegment(sketch, "E429", {"start": v(10.14, 7.71) * mm, "end": v(10.06, 7.57) * mm});
            skLineSegment(sketch, "E430", {"start": v(11.56, 6.22) * mm, "end": v(11.8, 6.82) * mm});
            skLineSegment(sketch, "E431", {"start": v(10.03, 7.1) * mm, "end": v(10.02, 6.85) * mm});
            skLineSegment(sketch, "E432", {"start": v(19.9, 4.08) * mm, "end": v(19.94, 4.1) * mm});
            skLineSegment(sketch, "E433", {"start": v(20.05, 4.19) * mm, "end": v(20.08, 4.18) * mm});
            skLineSegment(sketch, "E434", {"start": v(20.13, 4.13) * mm, "end": v(20.16, 4.1) * mm});
            skLineSegment(sketch, "E435", {"start": v(20.22, -2.67) * mm, "end": v(20.22, -2.71) * mm});
            skLineSegment(sketch, "E436", {"start": v(19.61, 3.83) * mm, "end": v(19.86, 4.05) * mm});
            skLineSegment(sketch, "E437", {"start": v(20.22, -2.71) * mm, "end": v(20.23, -2.79) * mm});
            skLineSegment(sketch, "E438", {"start": v(9.1, 5) * mm, "end": v(9.56, 5.07) * mm});
            skLineSegment(sketch, "E439", {"start": v(10.1, 5.21) * mm, "end": v(10.65, 5.44) * mm});
            skLineSegment(sketch, "E440", {"start": v(10.94, 8.08) * mm, "end": v(10.66, 8.06) * mm});
            skLineSegment(sketch, "E441", {"start": v(18.38, 3.3) * mm, "end": v(18.79, 3.42) * mm});
            skLineSegment(sketch, "E442", {"start": v(20.02, 4.16) * mm, "end": v(20.05, 4.19) * mm});
            skLineSegment(sketch, "E443", {"start": v(20.22, -0.69) * mm, "end": v(20.22, -1.77) * mm});
            skLineSegment(sketch, "E444", {"start": v(20.08, 4.18) * mm, "end": v(20.1, 4.16) * mm});
            skLineSegment(sketch, "E445", {"start": v(9.56, 5.07) * mm, "end": v(10.1, 5.21) * mm});
            skLineSegment(sketch, "E446", {"start": v(10.01, 7.45) * mm, "end": v(10, 7.37) * mm});
            skLineSegment(sketch, "E447", {"start": v(9.2, 5.37) * mm, "end": v(8.66, 4.96) * mm});
            skLineSegment(sketch, "E448", {"start": v(20.22, -2.48) * mm, "end": v(20.22, -2.67) * mm});
            skLineSegment(sketch, "E449", {"start": v(20.4, -3.1) * mm, "end": v(20.54, -3.18) * mm});
            skLineSegment(sketch, "E450", {"start": v(20.54, -3.18) * mm, "end": v(20.73, -3.23) * mm});
            skLineSegment(sketch, "E451", {"start": v(11.84, 7.1) * mm, "end": v(11.85, 7.24) * mm});
            skLineSegment(sketch, "E452", {"start": v(11.7, 7.76) * mm, "end": v(11.52, 7.92) * mm});
            skLineSegment(sketch, "E453", {"start": v(17.42, 3.18) * mm, "end": v(17.5, 3.18) * mm});
            skLineSegment(sketch, "E454", {"start": v(20.22, 1.87) * mm, "end": v(20.22, 0.59) * mm});
            skLineSegment(sketch, "E455", {"start": v(11.8, 6.82) * mm, "end": v(11.82, 7.02) * mm});
            skLineSegment(sketch, "E456", {"start": v(11.27, 8.03) * mm, "end": v(10.94, 8.08) * mm});
            skLineSegment(sketch, "E457", {"start": v(18.79, 3.42) * mm, "end": v(19.21, 3.6) * mm});
            skLineSegment(sketch, "E458", {"start": v(19.21, 3.6) * mm, "end": v(19.61, 3.83) * mm});
            skLineSegment(sketch, "E459", {"start": v(11.82, 7.02) * mm, "end": v(11.84, 7.1) * mm});
            skLineSegment(sketch, "E460", {"start": v(20.22, 3.78) * mm, "end": v(20.22, 3) * mm});
            skLineSegment(sketch, "E461", {"start": v(20.22, 3) * mm, "end": v(20.22, 1.87) * mm});
            skLineSegment(sketch, "E462", {"start": v(19.86, 4.05) * mm, "end": v(19.9, 4.08) * mm});
            skLineSegment(sketch, "E463", {"start": v(17.96, 2.4) * mm, "end": v(17.92, 2.46) * mm});
            skLineSegment(sketch, "E464", {"start": v(17.87, 2.53) * mm, "end": v(17.8, 2.61) * mm});
            skLineSegment(sketch, "E465", {"start": v(24.27, -3.64) * mm, "end": v(24.97, -3.64) * mm});
            skLineSegment(sketch, "E466", {"start": v(24.97, -3.64) * mm, "end": v(25.2, -3.64) * mm});
            skLineSegment(sketch, "E467", {"start": v(17.43, -3.27) * mm, "end": v(17.55, -3.26) * mm});
            skLineSegment(sketch, "E468", {"start": v(19.68, -3.7) * mm, "end": v(18.97, -3.7) * mm});
            skLineSegment(sketch, "E469", {"start": v(17.98, -2.5) * mm, "end": v(17.98, -1.85) * mm});
            skLineSegment(sketch, "E470", {"start": v(17.34, 2.82) * mm, "end": v(17.32, 2.89) * mm});
            skLineSegment(sketch, "E471", {"start": v(17.2, -3.33) * mm, "end": v(17.21, -3.29) * mm});
            skLineSegment(sketch, "E472", {"start": v(17.98, -2.8) * mm, "end": v(17.98, -2.77) * mm});
            skLineSegment(sketch, "E473", {"start": v(17.98, 2.37) * mm, "end": v(17.96, 2.4) * mm});
            skLineSegment(sketch, "E474", {"start": v(20.83, -3.69) * mm, "end": v(20.7, -3.7) * mm});
            skLineSegment(sketch, "E475", {"start": v(18.97, -3.7) * mm, "end": v(18.26, -3.7) * mm});
            skLineSegment(sketch, "E476", {"start": v(17.77, -3.17) * mm, "end": v(17.86, -3.1) * mm});
            skLineSegment(sketch, "E477", {"start": v(17.9, -3.04) * mm, "end": v(17.93, -2.99) * mm});
            skLineSegment(sketch, "E478", {"start": v(17.13, -3.61) * mm, "end": v(17.15, -3.54) * mm});
            skLineSegment(sketch, "E479", {"start": v(17.86, -3.1) * mm, "end": v(17.9, -3.04) * mm});
            skLineSegment(sketch, "E480", {"start": v(17.93, -2.99) * mm, "end": v(17.95, -2.93) * mm});
            skLineSegment(sketch, "E481", {"start": v(17.34, -3.28) * mm, "end": v(17.43, -3.27) * mm});
            skLineSegment(sketch, "E482", {"start": v(17.97, -2.84) * mm, "end": v(17.98, -2.8) * mm});
            skLineSegment(sketch, "E483", {"start": v(17.98, -1.85) * mm, "end": v(17.98, -0.96) * mm});
            skLineSegment(sketch, "E484", {"start": v(17.98, 0.03) * mm, "end": v(17.98, 0.99) * mm});
            skLineSegment(sketch, "E485", {"start": v(17.66, -3.22) * mm, "end": v(17.77, -3.17) * mm});
            skLineSegment(sketch, "E486", {"start": v(17.98, 1.78) * mm, "end": v(17.98, 2.27) * mm});
            skLineSegment(sketch, "E487", {"start": v(17.98, -0.96) * mm, "end": v(17.98, 0.03) * mm});
            skLineSegment(sketch, "E488", {"start": v(17.92, 2.46) * mm, "end": v(17.87, 2.53) * mm});
            skLineSegment(sketch, "E489", {"start": v(18.26, -3.7) * mm, "end": v(17.65, -3.7) * mm});
            skLineSegment(sketch, "E490", {"start": v(17.71, 2.69) * mm, "end": v(17.62, 2.74) * mm});
            skLineSegment(sketch, "E491", {"start": v(17.5, 2.77) * mm, "end": v(17.4, 2.78) * mm});
            skLineSegment(sketch, "E492", {"start": v(17.11, -3.69) * mm, "end": v(17.13, -3.61) * mm});
            skLineSegment(sketch, "E493", {"start": v(17.55, -3.26) * mm, "end": v(17.66, -3.22) * mm});
            skLineSegment(sketch, "E494", {"start": v(17.98, -2.77) * mm, "end": v(17.98, -2.5) * mm});
            skLineSegment(sketch, "E495", {"start": v(17.65, -3.7) * mm, "end": v(17.24, -3.7) * mm});
            skLineSegment(sketch, "E496", {"start": v(20.29, -3.7) * mm, "end": v(19.68, -3.7) * mm});
            skLineSegment(sketch, "E497", {"start": v(20.7, -3.7) * mm, "end": v(20.29, -3.7) * mm});
            skLineSegment(sketch, "E498", {"start": v(17.96, -2.88) * mm, "end": v(17.97, -2.84) * mm});
            skLineSegment(sketch, "E499", {"start": v(17.8, 2.61) * mm, "end": v(17.71, 2.69) * mm});
            skLineSegment(sketch, "E500", {"start": v(17.4, 2.78) * mm, "end": v(17.34, 2.82) * mm});
            skLineSegment(sketch, "E501", {"start": v(17.17, -3.46) * mm, "end": v(17.19, -3.39) * mm});
            skLineSegment(sketch, "E502", {"start": v(17.33, 2.97) * mm, "end": v(17.35, 3.04) * mm});
            skLineSegment(sketch, "E503", {"start": v(17.24, -3.7) * mm, "end": v(17.11, -3.69) * mm});
            skLineSegment(sketch, "E504", {"start": v(17.35, 3.04) * mm, "end": v(17.38, 3.11) * mm});
            skLineSegment(sketch, "E505", {"start": v(20.73, -3.23) * mm, "end": v(20.83, -3.24) * mm});
            skLineSegment(sketch, "E506", {"start": v(17.21, -3.29) * mm, "end": v(17.26, -3.28) * mm});
            skLineSegment(sketch, "E507", {"start": v(21.34, -3.64) * mm, "end": v(21.63, -3.64) * mm});
            skLineSegment(sketch, "E508", {"start": v(21.63, -3.64) * mm, "end": v(22.37, -3.64) * mm});
            skLineSegment(sketch, "E509", {"start": v(22.37, -3.64) * mm, "end": v(23.33, -3.64) * mm});
            skLineSegment(sketch, "E510", {"start": v(17.26, -3.28) * mm, "end": v(17.34, -3.28) * mm});
            skLineSegment(sketch, "E511", {"start": v(17.98, 2.27) * mm, "end": v(17.98, 2.37) * mm});
            skLineSegment(sketch, "E512", {"start": v(17.15, -3.54) * mm, "end": v(17.17, -3.46) * mm});
            skLineSegment(sketch, "E513", {"start": v(17.98, 0.99) * mm, "end": v(17.98, 1.78) * mm});
            skLineSegment(sketch, "E514", {"start": v(17.19, -3.39) * mm, "end": v(17.2, -3.33) * mm});
            skLineSegment(sketch, "E515", {"start": v(17.62, 2.74) * mm, "end": v(17.5, 2.77) * mm});
            skLineSegment(sketch, "E516", {"start": v(17.32, 2.89) * mm, "end": v(17.33, 2.97) * mm});
            skLineSegment(sketch, "E517", {"start": v(17.38, 3.11) * mm, "end": v(17.42, 3.18) * mm});
            skLineSegment(sketch, "E518", {"start": v(17.95, -2.93) * mm, "end": v(17.96, -2.88) * mm});
            skLineSegment(sketch, "E519", {"start": v(23.33, -3.64) * mm, "end": v(24.27, -3.64) * mm});
            skLineSegment(sketch, "E520", {"start": v(24.4, 2.08) * mm, "end": v(24.46, 2.26) * mm});
            skLineSegment(sketch, "E521", {"start": v(24.35, 4.26) * mm, "end": v(24.28, 4.28) * mm});
            skLineSegment(sketch, "E522", {"start": v(24.2, 4.3) * mm, "end": v(24.1, 4.33) * mm});
            skLineSegment(sketch, "E523", {"start": v(24.7, 2.72) * mm, "end": v(24.93, 2.95) * mm});
            skLineSegment(sketch, "E524", {"start": v(25.2, -3.5) * mm, "end": v(25.13, -3.47) * mm});
            skLineSegment(sketch, "E525", {"start": v(24.4, 1.85) * mm, "end": v(24.4, 1.97) * mm});
            skLineSegment(sketch, "E526", {"start": v(25.05, 3) * mm, "end": v(25.03, 2.8) * mm});
            skLineSegment(sketch, "E527", {"start": v(25.8, 1.72) * mm, "end": v(26.35, 1.75) * mm});
            skLineSegment(sketch, "E528", {"start": v(24.4, -2.14) * mm, "end": v(24.4, -1.1) * mm});
            skLineSegment(sketch, "E529", {"start": v(24.66, 3.66) * mm, "end": v(24.49, 3.42) * mm});
            skLineSegment(sketch, "E530", {"start": v(25.15, 2.15) * mm, "end": v(25.39, 1.87) * mm});
            skLineSegment(sketch, "E531", {"start": v(26.35, 1.75) * mm, "end": v(26.77, 1.94) * mm});
            skLineSegment(sketch, "E532", {"start": v(24.8, -3.35) * mm, "end": v(24.61, -3.2) * mm});
            skLineSegment(sketch, "E533", {"start": v(24.61, -3.2) * mm, "end": v(24.46, -2.97) * mm});
            skLineSegment(sketch, "E534", {"start": v(27.12, 3.99) * mm, "end": v(26.74, 4.25) * mm});
            skLineSegment(sketch, "E535", {"start": v(25.2, -3.52) * mm, "end": v(25.2, -3.5) * mm});
            skLineSegment(sketch, "E536", {"start": v(27.26, 2.51) * mm, "end": v(27.36, 2.75) * mm});
            skLineSegment(sketch, "E537", {"start": v(24.4, -2.73) * mm, "end": v(24.4, -2.14) * mm});
            skLineSegment(sketch, "E538", {"start": v(27.36, 2.75) * mm, "end": v(27.4, 2.87) * mm});
            skLineSegment(sketch, "E539", {"start": v(26.74, 4.25) * mm, "end": v(26.12, 4.3) * mm});
            skLineSegment(sketch, "E540", {"start": v(24.97, 3.92) * mm, "end": v(24.66, 3.66) * mm});
            skLineSegment(sketch, "E541", {"start": v(24.4, -1.1) * mm, "end": v(24.4, 0.09) * mm});
            skLineSegment(sketch, "E542", {"start": v(24.98, -3.43) * mm, "end": v(24.8, -3.35) * mm});
            skLineSegment(sketch, "E543", {"start": v(24.55, 2.48) * mm, "end": v(24.7, 2.72) * mm});
            skLineSegment(sketch, "E544", {"start": v(24.4, 4.25) * mm, "end": v(24.35, 4.26) * mm});
            skLineSegment(sketch, "E545", {"start": v(25.2, -3.56) * mm, "end": v(25.2, -3.52) * mm});
            skLineSegment(sketch, "E546", {"start": v(24.4, 1.17) * mm, "end": v(24.4, 1.85) * mm});
            skLineSegment(sketch, "E547", {"start": v(25.03, 2.8) * mm, "end": v(25.05, 2.49) * mm});
            skLineSegment(sketch, "E548", {"start": v(25.13, -3.47) * mm, "end": v(24.98, -3.43) * mm});
            skLineSegment(sketch, "E549", {"start": v(27.07, 2.22) * mm, "end": v(27.26, 2.51) * mm});
            skLineSegment(sketch, "E550", {"start": v(24.49, 3.42) * mm, "end": v(24.4, 3.24) * mm});
            skLineSegment(sketch, "E551", {"start": v(24.46, 2.26) * mm, "end": v(24.55, 2.48) * mm});
            skLineSegment(sketch, "E552", {"start": v(24.93, 2.95) * mm, "end": v(25.05, 3) * mm});
            skLineSegment(sketch, "E553", {"start": v(25.44, 4.15) * mm, "end": v(24.97, 3.92) * mm});
            skLineSegment(sketch, "E554", {"start": v(25.39, 1.87) * mm, "end": v(25.8, 1.72) * mm});
            skLineSegment(sketch, "E555", {"start": v(25.2, -3.6) * mm, "end": v(25.2, -3.56) * mm});
            skLineSegment(sketch, "E556", {"start": v(26.77, 1.94) * mm, "end": v(27.07, 2.22) * mm});
            skLineSegment(sketch, "E557", {"start": v(24.46, -2.97) * mm, "end": v(24.4, -2.73) * mm});
            skLineSegment(sketch, "E558", {"start": v(24.28, 4.28) * mm, "end": v(24.2, 4.3) * mm});
            skLineSegment(sketch, "E559", {"start": v(25.2, -3.64) * mm, "end": v(25.2, -3.6) * mm});
            skLineSegment(sketch, "E560", {"start": v(24.1, 4.33) * mm, "end": v(24.05, 4.35) * mm});
            skLineSegment(sketch, "E561", {"start": v(24.05, 4.35) * mm, "end": v(23.92, 4.2) * mm});
            skLineSegment(sketch, "E562", {"start": v(23.66, 3.94) * mm, "end": v(23.26, 3.65) * mm});
            skLineSegment(sketch, "E563", {"start": v(23.26, 3.65) * mm, "end": v(22.71, 3.4) * mm});
            skLineSegment(sketch, "E564", {"start": v(22.71, 3.4) * mm, "end": v(22.02, 3.3) * mm});
            skLineSegment(sketch, "E565", {"start": v(24.4, 1.97) * mm, "end": v(24.4, 2.08) * mm});
            skLineSegment(sketch, "E566", {"start": v(24.4, 0.09) * mm, "end": v(24.4, 1.17) * mm});
            skLineSegment(sketch, "E567", {"start": v(25.05, 2.49) * mm, "end": v(25.15, 2.15) * mm});
            skLineSegment(sketch, "E568", {"start": v(27.4, 2.96) * mm, "end": v(27.4, 3.24) * mm});
            skLineSegment(sketch, "E569", {"start": v(24.4, 4.2) * mm, "end": v(24.4, 4.25) * mm});
            skLineSegment(sketch, "E570", {"start": v(27.32, 3.62) * mm, "end": v(27.12, 3.99) * mm});
            skLineSegment(sketch, "E571", {"start": v(23.92, 4.2) * mm, "end": v(23.66, 3.94) * mm});
            skLineSegment(sketch, "E572", {"start": v(22.02, 3.3) * mm, "end": v(21.54, 3.33) * mm});
            skLineSegment(sketch, "E573", {"start": v(27.4, 2.87) * mm, "end": v(27.4, 2.96) * mm});
            skLineSegment(sketch, "E574", {"start": v(27.4, 3.24) * mm, "end": v(27.32, 3.62) * mm});
            skLineSegment(sketch, "E575", {"start": v(26.12, 4.3) * mm, "end": v(25.44, 4.15) * mm});
            skLineSegment(sketch, "E576", {"start": v(21.54, 3.33) * mm, "end": v(21.5, 3.29) * mm});
            skLineSegment(sketch, "E577", {"start": v(21.5, 3.29) * mm, "end": v(21.47, 3.21) * mm});
            skLineSegment(sketch, "E578", {"start": v(-11.45, -0.72) * mm, "end": v(-11.55, -1.68) * mm});
            skLineSegment(sketch, "E579", {"start": v(21.32, -3.35) * mm, "end": v(21.3, -3.44) * mm});
            skLineSegment(sketch, "E580", {"start": v(-13.14, 3.25) * mm, "end": v(-12.66, 2.85) * mm});
            skLineSegment(sketch, "E581", {"start": v(-14.9, 2.9) * mm, "end": v(-15.14, 2.72) * mm});
            skLineSegment(sketch, "E582", {"start": v(22.25, 0.47) * mm, "end": v(22.25, -0.93) * mm});
            skLineSegment(sketch, "E583", {"start": v(21.47, 3.21) * mm, "end": v(21.43, 3.12) * mm});
            skLineSegment(sketch, "E584", {"start": v(-13.52, -4.3) * mm, "end": v(-14.1, -4.46) * mm});
            skLineSegment(sketch, "E585", {"start": v(-15.14, 2.72) * mm, "end": v(-15.35, 2.41) * mm});
            skLineSegment(sketch, "E586", {"start": v(21.49, 2.95) * mm, "end": v(21.61, 2.9) * mm});
            skLineSegment(sketch, "E587", {"start": v(-15.35, 2.41) * mm, "end": v(-15.54, 2.02) * mm});
            skLineSegment(sketch, "E588", {"start": v(-14.23, 3.67) * mm, "end": v(-13.67, 3.53) * mm});
            skLineSegment(sketch, "E589", {"start": v(-12.1, -3.14) * mm, "end": v(-12.5, -3.66) * mm});
            skLineSegment(sketch, "E590", {"start": v(-17.87, -0.83) * mm, "end": v(-17.84, 0.05) * mm});
            skLineSegment(sketch, "E591", {"start": v(21.51, -3.29) * mm, "end": v(21.38, -3.3) * mm});
            skLineSegment(sketch, "E592", {"start": v(21.61, 2.9) * mm, "end": v(21.77, 2.87) * mm});
            skLineSegment(sketch, "E593", {"start": v(21.3, -3.44) * mm, "end": v(21.3, -3.53) * mm});
            skLineSegment(sketch, "E594", {"start": v(-14.68, -4.5) * mm, "end": v(-15.27, -4.45) * mm});
            skLineSegment(sketch, "E595", {"start": v(-17.39, 1.62) * mm, "end": v(-17, 2.26) * mm});
            skLineSegment(sketch, "E596", {"start": v(-13.67, 3.53) * mm, "end": v(-13.14, 3.25) * mm});
            skLineSegment(sketch, "E597", {"start": v(21.77, 2.87) * mm, "end": v(21.93, 2.84) * mm});
            skLineSegment(sketch, "E598", {"start": v(21.93, 2.84) * mm, "end": v(22.08, 2.83) * mm});
            skLineSegment(sketch, "E599", {"start": v(22.25, 2.83) * mm, "end": v(22.25, 2.64) * mm});
            skLineSegment(sketch, "E600", {"start": v(22.08, 2.83) * mm, "end": v(22.19, 2.83) * mm});
            skLineSegment(sketch, "E601", {"start": v(22.25, 2.64) * mm, "end": v(22.25, 1.76) * mm});
            skLineSegment(sketch, "E602", {"start": v(22.25, -2.7) * mm, "end": v(22.23, -2.75) * mm});
            skLineSegment(sketch, "E603", {"start": v(21.43, 3.12) * mm, "end": v(21.43, 3.03) * mm});
            skLineSegment(sketch, "E604", {"start": v(22.25, -0.93) * mm, "end": v(22.25, -2.1) * mm});
            skLineSegment(sketch, "E605", {"start": v(21.3, -3.53) * mm, "end": v(21.33, -3.6) * mm});
            skLineSegment(sketch, "E606", {"start": v(22.23, -2.75) * mm, "end": v(22.16, -2.85) * mm});
            skLineSegment(sketch, "E607", {"start": v(-16.83, -3.54) * mm, "end": v(-17.24, -3.01) * mm});
            skLineSegment(sketch, "E608", {"start": v(-11.55, -1.68) * mm, "end": v(-11.77, -2.49) * mm});
            skLineSegment(sketch, "E609", {"start": v(21.43, 3.03) * mm, "end": v(21.49, 2.95) * mm});
            skLineSegment(sketch, "E610", {"start": v(22.19, 2.83) * mm, "end": v(22.25, 2.83) * mm});
            skLineSegment(sketch, "E611", {"start": v(-17.56, -2.38) * mm, "end": v(-17.77, -1.65) * mm});
            skLineSegment(sketch, "E612", {"start": v(22.03, -3) * mm, "end": v(21.87, -3.14) * mm});
            skLineSegment(sketch, "E613", {"start": v(-12.5, -3.66) * mm, "end": v(-12.99, -4.04) * mm});
            skLineSegment(sketch, "E614", {"start": v(-12.99, -4.04) * mm, "end": v(-13.52, -4.3) * mm});
            skLineSegment(sketch, "E615", {"start": v(-14.1, -4.46) * mm, "end": v(-14.68, -4.5) * mm});
            skLineSegment(sketch, "E616", {"start": v(-16.02, 3.23) * mm, "end": v(-15.44, 3.52) * mm});
            skLineSegment(sketch, "E617", {"start": v(21.33, -3.6) * mm, "end": v(21.34, -3.64) * mm});
            skLineSegment(sketch, "E618", {"start": v(22.16, -2.85) * mm, "end": v(22.03, -3) * mm});
            skLineSegment(sketch, "E619", {"start": v(-15.27, -4.45) * mm, "end": v(-15.83, -4.26) * mm});
            skLineSegment(sketch, "E620", {"start": v(-16.36, -3.95) * mm, "end": v(-16.83, -3.54) * mm});
            skLineSegment(sketch, "E621", {"start": v(-14.83, 3.67) * mm, "end": v(-14.23, 3.67) * mm});
            skLineSegment(sketch, "E622", {"start": v(-15.44, 3.52) * mm, "end": v(-14.83, 3.67) * mm});
            skLineSegment(sketch, "E623", {"start": v(-11.77, -2.49) * mm, "end": v(-12.1, -3.14) * mm});
            skLineSegment(sketch, "E624", {"start": v(-15.83, -4.26) * mm, "end": v(-16.36, -3.95) * mm});
            skLineSegment(sketch, "E625", {"start": v(21.87, -3.14) * mm, "end": v(21.7, -3.25) * mm});
            skLineSegment(sketch, "E626", {"start": v(-17.24, -3.01) * mm, "end": v(-17.56, -2.38) * mm});
            skLineSegment(sketch, "E627", {"start": v(-17.67, 0.88) * mm, "end": v(-17.39, 1.62) * mm});
            skLineSegment(sketch, "E628", {"start": v(22.25, 1.76) * mm, "end": v(22.25, 0.47) * mm});
            skLineSegment(sketch, "E629", {"start": v(-17, 2.26) * mm, "end": v(-16.54, 2.8) * mm});
            skLineSegment(sketch, "E630", {"start": v(-17.84, 0.05) * mm, "end": v(-17.67, 0.88) * mm});
            skLineSegment(sketch, "E631", {"start": v(-16.54, 2.8) * mm, "end": v(-16.02, 3.23) * mm});
            skLineSegment(sketch, "E632", {"start": v(-12.23, 2.34) * mm, "end": v(-11.89, 1.72) * mm});
            skLineSegment(sketch, "E633", {"start": v(-17.77, -1.65) * mm, "end": v(-17.87, -0.83) * mm});
            skLineSegment(sketch, "E634", {"start": v(-11.63, 1) * mm, "end": v(-11.48, 0.2) * mm});
            skLineSegment(sketch, "E635", {"start": v(-14.65, 2.97) * mm, "end": v(-14.9, 2.9) * mm});
            skLineSegment(sketch, "E636", {"start": v(21.7, -3.25) * mm, "end": v(21.51, -3.29) * mm});
            skLineSegment(sketch, "E637", {"start": v(22.25, -2.1) * mm, "end": v(22.25, -2.7) * mm});
            skLineSegment(sketch, "E638", {"start": v(21.38, -3.3) * mm, "end": v(21.32, -3.35) * mm});
            skLineSegment(sketch, "E639", {"start": v(-12.66, 2.85) * mm, "end": v(-12.23, 2.34) * mm});
            skLineSegment(sketch, "E640", {"start": v(-11.89, 1.72) * mm, "end": v(-11.63, 1) * mm});
            skLineSegment(sketch, "E641", {"start": v(-11.48, 0.2) * mm, "end": v(-11.45, -0.72) * mm});
            skLineSegment(sketch, "E642", {"start": v(-14.16, 2.72) * mm, "end": v(-14.4, 2.9) * mm});
            skLineSegment(sketch, "E643", {"start": v(-13.53, -2.23) * mm, "end": v(-13.43, -1.64) * mm});
            skLineSegment(sketch, "E644", {"start": v(-15.02, -3.8) * mm, "end": v(-14.78, -3.92) * mm});
            skLineSegment(sketch, "E645", {"start": v(-15.54, 2.02) * mm, "end": v(-15.7, 1.53) * mm});
            skLineSegment(sketch, "E646", {"start": v(-14.27, -3.8) * mm, "end": v(-14.05, -3.55) * mm});
            skLineSegment(sketch, "E647", {"start": v(-14.05, -3.55) * mm, "end": v(-13.84, -3.2) * mm});
            skLineSegment(sketch, "E648", {"start": v(-13.43, -1.64) * mm, "end": v(-13.37, -1) * mm});
            skLineSegment(sketch, "E649", {"start": v(-13.6, 1.53) * mm, "end": v(-13.75, 2.02) * mm});
            skLineSegment(sketch, "E650", {"start": v(-14.78, -3.92) * mm, "end": v(-14.52, -3.92) * mm});
            skLineSegment(sketch, "E651", {"start": v(-15.63, -2.75) * mm, "end": v(-15.45, -3.2) * mm});
            skLineSegment(sketch, "E652", {"start": v(-13.37, -1) * mm, "end": v(-13.35, -0.31) * mm});
            skLineSegment(sketch, "E653", {"start": v(-15.45, -3.2) * mm, "end": v(-15.25, -3.55) * mm});
            skLineSegment(sketch, "E654", {"start": v(-13.47, 0.97) * mm, "end": v(-13.6, 1.53) * mm});
            skLineSegment(sketch, "E655", {"start": v(-15.25, -3.55) * mm, "end": v(-15.02, -3.8) * mm});
            skLineSegment(sketch, "E656", {"start": v(-13.35, -0.31) * mm, "end": v(-13.39, 0.35) * mm});
            skLineSegment(sketch, "E657", {"start": v(-13.67, -2.75) * mm, "end": v(-13.53, -2.23) * mm});
            skLineSegment(sketch, "E658", {"start": v(-15.93, -1) * mm, "end": v(-15.87, -1.64) * mm});
            skLineSegment(sketch, "E659", {"start": v(-13.84, -3.2) * mm, "end": v(-13.67, -2.75) * mm});
            skLineSegment(sketch, "E660", {"start": v(-14.4, 2.9) * mm, "end": v(-14.65, 2.97) * mm});
            skLineSegment(sketch, "E661", {"start": v(-13.39, 0.35) * mm, "end": v(-13.47, 0.97) * mm});
            skLineSegment(sketch, "E662", {"start": v(-15.94, -0.31) * mm, "end": v(-15.93, -1) * mm});
            skLineSegment(sketch, "E663", {"start": v(-15.7, 1.53) * mm, "end": v(-15.82, 0.97) * mm});
            skLineSegment(sketch, "E664", {"start": v(-15.9, 0.35) * mm, "end": v(-15.94, -0.31) * mm});
            skLineSegment(sketch, "E665", {"start": v(-15.82, 0.97) * mm, "end": v(-15.9, 0.35) * mm});
            skLineSegment(sketch, "E666", {"start": v(-14.52, -3.92) * mm, "end": v(-14.27, -3.8) * mm});
            skLineSegment(sketch, "E667", {"start": v(-13.94, 2.41) * mm, "end": v(-14.16, 2.72) * mm});
            skLineSegment(sketch, "E668", {"start": v(-15.87, -1.64) * mm, "end": v(-15.77, -2.23) * mm});
            skLineSegment(sketch, "E669", {"start": v(-15.77, -2.23) * mm, "end": v(-15.63, -2.75) * mm});
            skLineSegment(sketch, "E670", {"start": v(-13.75, 2.02) * mm, "end": v(-13.94, 2.41) * mm});
            skLineSegment(sketch, "E671", {"start": v(-2.77, 6.96) * mm, "end": v(-2.76, 7.03) * mm});
            skLineSegment(sketch, "E672", {"start": v(-2.83, 6.72) * mm, "end": v(-2.81, 6.8) * mm});
            skLineSegment(sketch, "E673", {"start": v(-2.76, 7.03) * mm, "end": v(-2.75, 7.07) * mm});
            skLineSegment(sketch, "E674", {"start": v(-2.85, 6.64) * mm, "end": v(-2.83, 6.72) * mm});
            skLineSegment(sketch, "E675", {"start": v(-2.81, 6.8) * mm, "end": v(-2.8, 6.88) * mm});
            skLineSegment(sketch, "E676", {"start": v(-2.8, 6.88) * mm, "end": v(-2.77, 6.96) * mm});
            skLineSegment(sketch, "E677", {"start": v(5.65, 3.38) * mm, "end": v(5.81, 2.55) * mm});
            skLineSegment(sketch, "E678", {"start": v(-11.66, -3.8) * mm, "end": v(-11.37, -3.69) * mm});
            skLineSegment(sketch, "E679", {"start": v(-11.37, -3.69) * mm, "end": v(-11.09, -3.48) * mm});
            skLineSegment(sketch, "E680", {"start": v(-11.53, 2.48) * mm, "end": v(-11.52, 2.54) * mm});
            skLineSegment(sketch, "E681", {"start": v(-8.17, -4) * mm, "end": v(-8.17, -4.08) * mm});
            skLineSegment(sketch, "E682", {"start": v(-11.52, 2.63) * mm, "end": v(-11.5, 2.7) * mm});
            skLineSegment(sketch, "E683", {"start": v(1.76, 7.08) * mm, "end": v(1.95, 7.07) * mm});
            skLineSegment(sketch, "E684", {"start": v(3.63, 6.48) * mm, "end": v(4.17, 6.03) * mm});
            skLineSegment(sketch, "E685", {"start": v(-10.91, -2.3) * mm, "end": v(-10.92, -1.05) * mm});
            skLineSegment(sketch, "E686", {"start": v(-11.09, -3.48) * mm, "end": v(-10.94, -3.13) * mm});
            skLineSegment(sketch, "E687", {"start": v(-10.93, 1.59) * mm, "end": v(-10.98, 2.07) * mm});
            skLineSegment(sketch, "E688", {"start": v(-9.01, 2.98) * mm, "end": v(-9.01, 2.64) * mm});
            skLineSegment(sketch, "E689", {"start": v(-11.24, 2.4) * mm, "end": v(-11.33, 2.43) * mm});
            skLineSegment(sketch, "E690", {"start": v(-11.81, -3.85) * mm, "end": v(-11.8, -3.82) * mm});
            skLineSegment(sketch, "E691", {"start": v(-11.33, 2.43) * mm, "end": v(-11.42, 2.46) * mm});
            skLineSegment(sketch, "E692", {"start": v(4.65, 5.5) * mm, "end": v(5.06, 4.86) * mm});
            skLineSegment(sketch, "E693", {"start": v(5.4, 4.15) * mm, "end": v(5.65, 3.38) * mm});
            skLineSegment(sketch, "E694", {"start": v(5.81, 2.55) * mm, "end": v(5.88, 1.67) * mm});
            skLineSegment(sketch, "E695", {"start": v(5.88, 1.67) * mm, "end": v(5.87, 0.92) * mm});
            skLineSegment(sketch, "E696", {"start": v(5.87, 0.92) * mm, "end": v(5.8, 0.22) * mm});
            skLineSegment(sketch, "E697", {"start": v(5.8, 0.22) * mm, "end": v(5.67, -0.47) * mm});
            skLineSegment(sketch, "E698", {"start": v(5.67, -0.47) * mm, "end": v(5.49, -1.14) * mm});
            skLineSegment(sketch, "E699", {"start": v(-10.98, 2.07) * mm, "end": v(-11.12, 2.37) * mm});
            skLineSegment(sketch, "E700", {"start": v(1.59, 7.09) * mm, "end": v(1.76, 7.08) * mm});
            skLineSegment(sketch, "E701", {"start": v(-9.25, -4.1) * mm, "end": v(-10.53, -4.1) * mm});
            skLineSegment(sketch, "E702", {"start": v(-8.17, -4.08) * mm, "end": v(-8.31, -4.1) * mm});
            skLineSegment(sketch, "E703", {"start": v(5.25, -1.76) * mm, "end": v(4.96, -2.35) * mm});
            skLineSegment(sketch, "E704", {"start": v(-11.81, -4.03) * mm, "end": v(-11.81, -3.94) * mm});
            skLineSegment(sketch, "E705", {"start": v(-10.53, -4.1) * mm, "end": v(-11.56, -4.1) * mm});
            skLineSegment(sketch, "E706", {"start": v(-9, 3.32) * mm, "end": v(-9.01, 2.98) * mm});
            skLineSegment(sketch, "E707", {"start": v(-10.9, 2.97) * mm, "end": v(-10, 3.32) * mm});
            skLineSegment(sketch, "E708", {"start": v(2.54, 6.96) * mm, "end": v(2.73, 6.9) * mm});
            skLineSegment(sketch, "E709", {"start": v(3.1, 6.77) * mm, "end": v(3.63, 6.48) * mm});
            skLineSegment(sketch, "E710", {"start": v(-10.93, 1.09) * mm, "end": v(-10.93, 1.59) * mm});
            skLineSegment(sketch, "E711", {"start": v(-11.81, -4.1) * mm, "end": v(-11.81, -4.03) * mm});
            skLineSegment(sketch, "E712", {"start": v(-11.5, 2.7) * mm, "end": v(-11.46, 2.74) * mm});
            skLineSegment(sketch, "E713", {"start": v(-11.5, 2.47) * mm, "end": v(-11.53, 2.48) * mm});
            skLineSegment(sketch, "E714", {"start": v(2.14, 7.04) * mm, "end": v(2.34, 7) * mm});
            skLineSegment(sketch, "E715", {"start": v(2.73, 6.9) * mm, "end": v(2.92, 6.85) * mm});
            skLineSegment(sketch, "E716", {"start": v(-11.46, 2.74) * mm, "end": v(-10.9, 2.97) * mm});
            skLineSegment(sketch, "E717", {"start": v(-11.56, -4.1) * mm, "end": v(-11.81, -4.1) * mm});
            skLineSegment(sketch, "E718", {"start": v(-9.01, 2.64) * mm, "end": v(-9.01, 2.3) * mm});
            skLineSegment(sketch, "E719", {"start": v(-11.52, 2.54) * mm, "end": v(-11.52, 2.63) * mm});
            skLineSegment(sketch, "E720", {"start": v(-11.42, 2.46) * mm, "end": v(-11.5, 2.47) * mm});
            skLineSegment(sketch, "E721", {"start": v(-8.97, 3.67) * mm, "end": v(-9, 3.32) * mm});
            skLineSegment(sketch, "E722", {"start": v(2.34, 7) * mm, "end": v(2.54, 6.96) * mm});
            skLineSegment(sketch, "E723", {"start": v(2.92, 6.85) * mm, "end": v(3.1, 6.77) * mm});
            skLineSegment(sketch, "E724", {"start": v(-10.92, -1.05) * mm, "end": v(-10.93, 0.14) * mm});
            skLineSegment(sketch, "E725", {"start": v(4.17, 6.03) * mm, "end": v(4.65, 5.5) * mm});
            skLineSegment(sketch, "E726", {"start": v(5.06, 4.86) * mm, "end": v(5.4, 4.15) * mm});
            skLineSegment(sketch, "E727", {"start": v(5.49, -1.14) * mm, "end": v(5.25, -1.76) * mm});
            skLineSegment(sketch, "E728", {"start": v(-10, 3.32) * mm, "end": v(-9.23, 3.62) * mm});
            skLineSegment(sketch, "E729", {"start": v(4.96, -2.35) * mm, "end": v(4.63, -2.87) * mm});
            skLineSegment(sketch, "E730", {"start": v(-11.12, 2.37) * mm, "end": v(-11.24, 2.4) * mm});
            skLineSegment(sketch, "E731", {"start": v(-10.93, 0.14) * mm, "end": v(-10.94, 0.77) * mm});
            skLineSegment(sketch, "E732", {"start": v(-9.23, 3.62) * mm, "end": v(-8.97, 3.67) * mm});
            skLineSegment(sketch, "E733", {"start": v(4.63, -2.87) * mm, "end": v(4.24, -3.32) * mm});
            skLineSegment(sketch, "E734", {"start": v(4.24, -3.32) * mm, "end": v(3.91, -3.61) * mm});
            skLineSegment(sketch, "E735", {"start": v(-11.81, -3.94) * mm, "end": v(-11.81, -3.85) * mm});
            skLineSegment(sketch, "E736", {"start": v(-8.31, -4.1) * mm, "end": v(-9.25, -4.1) * mm});
            skLineSegment(sketch, "E737", {"start": v(-11.8, -3.82) * mm, "end": v(-11.66, -3.8) * mm});
            skLineSegment(sketch, "E738", {"start": v(-10.94, -3.13) * mm, "end": v(-10.91, -2.3) * mm});
            skLineSegment(sketch, "E739", {"start": v(1.95, 7.07) * mm, "end": v(2.14, 7.04) * mm});
            skLineSegment(sketch, "E740", {"start": v(-10.94, 0.77) * mm, "end": v(-10.93, 1.09) * mm});
            skLineSegment(sketch, "E741", {"start": v(-1.8, -0.96) * mm, "end": v(-1.8, 0.48) * mm});
            skLineSegment(sketch, "E742", {"start": v(-2.74, -4.25) * mm, "end": v(-2.74, -4.22) * mm});
            skLineSegment(sketch, "E743", {"start": v(1.6, -4.25) * mm, "end": v(1.22, -4.25) * mm});
            skLineSegment(sketch, "E744", {"start": v(-0.98, -4.25) * mm, "end": v(-1.74, -4.25) * mm});
            skLineSegment(sketch, "E745", {"start": v(-2.74, -4.17) * mm, "end": v(-2.74, -4.11) * mm});
            skLineSegment(sketch, "E746", {"start": v(-1.82, -2.86) * mm, "end": v(-1.8, -2.12) * mm});
            skLineSegment(sketch, "E747", {"start": v(-2.37, 6.56) * mm, "end": v(-2.56, 6.6) * mm});
            skLineSegment(sketch, "E748", {"start": v(-1.81, 3.5) * mm, "end": v(-1.82, 4.78) * mm});
            skLineSegment(sketch, "E749", {"start": v(-1.83, 6.06) * mm, "end": v(-1.89, 6.24) * mm});
            skLineSegment(sketch, "E750", {"start": v(-2.75, 7.07) * mm, "end": v(-2.53, 7.09) * mm});
            skLineSegment(sketch, "E751", {"start": v(-1.82, 5.68) * mm, "end": v(-1.83, 6.06) * mm});
            skLineSegment(sketch, "E752", {"start": v(1.8, -4.25) * mm, "end": v(1.6, -4.25) * mm});
            skLineSegment(sketch, "E753", {"start": v(3.91, -3.61) * mm, "end": v(3.63, -3.8) * mm});
            skLineSegment(sketch, "E754", {"start": v(-2.08, -3.54) * mm, "end": v(-1.95, -3.37) * mm});
            skLineSegment(sketch, "E755", {"start": v(2.73, -4.15) * mm, "end": v(2.42, -4.2) * mm});
            skLineSegment(sketch, "E756", {"start": v(-2.82, 6.64) * mm, "end": v(-2.85, 6.64) * mm});
            skLineSegment(sketch, "E757", {"start": v(-2.53, 7.09) * mm, "end": v(-2.03, 7.09) * mm});
            skLineSegment(sketch, "E758", {"start": v(2.11, -4.24) * mm, "end": v(1.8, -4.25) * mm});
            skLineSegment(sketch, "E759", {"start": v(-0.55, 7.09) * mm, "end": v(0.24, 7.09) * mm});
            skLineSegment(sketch, "E760", {"start": v(-2.7, -4.25) * mm, "end": v(-2.74, -4.25) * mm});
            skLineSegment(sketch, "E761", {"start": v(0.24, 7.09) * mm, "end": v(0.92, 7.09) * mm});
            skLineSegment(sketch, "E762", {"start": v(0.92, 7.09) * mm, "end": v(1.4, 7.09) * mm});
            skLineSegment(sketch, "E763", {"start": v(-0.17, -4.25) * mm, "end": v(-0.98, -4.25) * mm});
            skLineSegment(sketch, "E764", {"start": v(-2.24, -3.68) * mm, "end": v(-2.08, -3.54) * mm});
            skLineSegment(sketch, "E765", {"start": v(1.4, 7.09) * mm, "end": v(1.59, 7.09) * mm});
            skLineSegment(sketch, "E766", {"start": v(2.42, -4.2) * mm, "end": v(2.11, -4.24) * mm});
            skLineSegment(sketch, "E767", {"start": v(-2.56, -3.84) * mm, "end": v(-2.4, -3.78) * mm});
            skLineSegment(sketch, "E768", {"start": v(-1.85, -3.15) * mm, "end": v(-1.82, -2.86) * mm});
            skLineSegment(sketch, "E769", {"start": v(-2.03, 7.09) * mm, "end": v(-1.34, 7.09) * mm});
            skLineSegment(sketch, "E770", {"start": v(3.33, -3.96) * mm, "end": v(3.04, -4.07) * mm});
            skLineSegment(sketch, "E771", {"start": v(-1.8, 2.02) * mm, "end": v(-1.81, 3.5) * mm});
            skLineSegment(sketch, "E772", {"start": v(-1.34, 7.09) * mm, "end": v(-0.55, 7.09) * mm});
            skLineSegment(sketch, "E773", {"start": v(-2.74, -4.11) * mm, "end": v(-2.74, -4.05) * mm});
            skLineSegment(sketch, "E774", {"start": v(0.66, -3.04) * mm, "end": v(0.7, -3.22) * mm});
            skLineSegment(sketch, "E775", {"start": v(3.63, -3.8) * mm, "end": v(3.33, -3.96) * mm});
            skLineSegment(sketch, "E776", {"start": v(1.22, -4.25) * mm, "end": v(0.6, -4.25) * mm});
            skLineSegment(sketch, "E777", {"start": v(-2.02, 6.38) * mm, "end": v(-2.19, 6.49) * mm});
            skLineSegment(sketch, "E778", {"start": v(-1.8, 0.48) * mm, "end": v(-1.8, 2.02) * mm});
            skLineSegment(sketch, "E779", {"start": v(-1.82, 4.78) * mm, "end": v(-1.82, 5.68) * mm});
            skLineSegment(sketch, "E780", {"start": v(-2.74, -3.99) * mm, "end": v(-2.74, -3.94) * mm});
            skLineSegment(sketch, "E781", {"start": v(-2.19, 6.49) * mm, "end": v(-2.37, 6.56) * mm});
            skLineSegment(sketch, "E782", {"start": v(0.6, -4.25) * mm, "end": v(-0.17, -4.25) * mm});
            skLineSegment(sketch, "E783", {"start": v(3.04, -4.07) * mm, "end": v(2.73, -4.15) * mm});
            skLineSegment(sketch, "E784", {"start": v(-2.67, -3.89) * mm, "end": v(-2.56, -3.84) * mm});
            skLineSegment(sketch, "E785", {"start": v(-1.8, -2.12) * mm, "end": v(-1.8, -0.96) * mm});
            skLineSegment(sketch, "E786", {"start": v(-2.56, 6.6) * mm, "end": v(-2.71, 6.63) * mm});
            skLineSegment(sketch, "E787", {"start": v(-2.35, -4.25) * mm, "end": v(-2.7, -4.25) * mm});
            skLineSegment(sketch, "E788", {"start": v(-2.4, -3.78) * mm, "end": v(-2.24, -3.68) * mm});
            skLineSegment(sketch, "E789", {"start": v(-2.71, 6.63) * mm, "end": v(-2.82, 6.64) * mm});
            skLineSegment(sketch, "E790", {"start": v(-1.74, -4.25) * mm, "end": v(-2.35, -4.25) * mm});
            skLineSegment(sketch, "E791", {"start": v(-2.74, -4.05) * mm, "end": v(-2.74, -3.99) * mm});
            skLineSegment(sketch, "E792", {"start": v(-2.74, -3.94) * mm, "end": v(-2.74, -3.91) * mm});
            skLineSegment(sketch, "E793", {"start": v(-2.74, -4.22) * mm, "end": v(-2.74, -4.17) * mm});
            skLineSegment(sketch, "E794", {"start": v(-2.74, -3.91) * mm, "end": v(-2.67, -3.89) * mm});
            skLineSegment(sketch, "E795", {"start": v(-1.89, 6.24) * mm, "end": v(-2.02, 6.38) * mm});
            skLineSegment(sketch, "E796", {"start": v(-1.95, -3.37) * mm, "end": v(-1.85, -3.15) * mm});
            skLineSegment(sketch, "E797", {"start": v(8.61, 0.53) * mm, "end": v(8.88, 0.53) * mm});
            skLineSegment(sketch, "E798", {"start": v(11.45, 0.23) * mm, "end": v(11.72, 0.23) * mm});
            skLineSegment(sketch, "E799", {"start": v(9.7, 0.53) * mm, "end": v(9.87, 0.53) * mm});
            skLineSegment(sketch, "E800", {"start": v(9.45, 0.53) * mm, "end": v(9.7, 0.53) * mm});
            skLineSegment(sketch, "E801", {"start": v(10.98, 0.23) * mm, "end": v(11.45, 0.23) * mm});
            skLineSegment(sketch, "E802", {"start": v(8.88, 0.53) * mm, "end": v(9.17, 0.53) * mm});
            skLineSegment(sketch, "E803", {"start": v(9.17, 0.53) * mm, "end": v(9.45, 0.53) * mm});
            skLineSegment(sketch, "E804", {"start": v(9.87, 0.53) * mm, "end": v(9.94, 0.53) * mm});
            skLineSegment(sketch, "E805", {"start": v(8.38, 0.23) * mm, "end": v(8.68, 0.23) * mm});
            skLineSegment(sketch, "E806", {"start": v(8.41, 0.53) * mm, "end": v(8.61, 0.53) * mm});
            skLineSegment(sketch, "E807", {"start": v(8.68, 0.23) * mm, "end": v(9.16, 0.23) * mm});
            skLineSegment(sketch, "E808", {"start": v(10.4, 0.23) * mm, "end": v(10.98, 0.23) * mm});
            skLineSegment(sketch, "E809", {"start": v(9.76, 0.23) * mm, "end": v(10.4, 0.23) * mm});
            skLineSegment(sketch, "E810", {"start": v(9.16, 0.23) * mm, "end": v(9.76, 0.23) * mm});
            skLineSegment(sketch, "E811", {"start": v(20.83, -3.24) * mm, "end": v(20.83, -3.28) * mm});
            skLineSegment(sketch, "E812", {"start": v(20.83, -3.28) * mm, "end": v(20.83, -3.35) * mm});
            skLineSegment(sketch, "E813", {"start": v(20.83, -3.35) * mm, "end": v(20.83, -3.43) * mm});
            skLineSegment(sketch, "E814", {"start": v(20.83, -3.66) * mm, "end": v(20.83, -3.69) * mm});
            skLineSegment(sketch, "E815", {"start": v(20.83, -3.43) * mm, "end": v(20.83, -3.52) * mm});
            skLineSegment(sketch, "E816", {"start": v(20.83, -3.6) * mm, "end": v(20.83, -3.66) * mm});
            skLineSegment(sketch, "E817", {"start": v(20.83, -3.52) * mm, "end": v(20.83, -3.6) * mm});
            skLineSegment(sketch, "E818", {"start": v(24.4, 4.2) * mm, "end": v(24.4, 4) * mm});
            skLineSegment(sketch, "E819", {"start": v(24.4, 3.27) * mm, "end": v(24.4, 3.24) * mm});
            skLineSegment(sketch, "E820", {"start": v(24.4, 3.48) * mm, "end": v(24.4, 3.27) * mm});
            skLineSegment(sketch, "E821", {"start": v(24.4, 4) * mm, "end": v(24.4, 3.75) * mm});
            skLineSegment(sketch, "E822", {"start": v(24.4, 3.75) * mm, "end": v(24.4, 3.48) * mm});
            skLineSegment(sketch, "E823", {"start": v(24.4, 3.24) * mm, "end": v(24.4, 3.18) * mm});
            skLineSegment(sketch, "E824", {"start": v(-24.64, -3.75) * mm, "end": v(-24.64, -3.8) * mm});
            skLineSegment(sketch, "E825", {"start": v(-24.64, -3.8) * mm, "end": v(-24.64, -3.93) * mm});
            skLineSegment(sketch, "E826", {"start": v(-24.64, -3.93) * mm, "end": v(-24.64, -4.04) * mm});
            skLineSegment(sketch, "E827", {"start": v(-24.64, -4.04) * mm, "end": v(-24.64, -4.1) * mm});
            skSolve(sketch);
        }
        {
            var Q0;
            Q0 = qSketchRegion(id + "F0", true);
            extrude(context, id + "F1", {"entities" : qUnion([Q0]), "endBound" : BoundingType.SYMMETRIC, "depth" : 30 * mm});
        }
        {
            var Q0;
            Q0=qCreatedBy(makeId("Front.planeOp"),FACE);
            var sketch = newSketch(context, id + "F2", { "sketchPlane" : qUnion([Q0])});
            skLineSegment(sketch, "E828", {"start": v(-14.1, -12.03) * mm, "end": v(-13.6, -15.18) * mm});
            skLineSegment(sketch, "E829", {"start": v(-10.42, 14.47) * mm, "end": v(-7.07, 15.14) * mm});
            skLineSegment(sketch, "E830", {"start": v(28.93, 0.92) * mm, "end": v(28.7, 2.84) * mm});
            skLineSegment(sketch, "E831", {"start": v(28.7, 2.84) * mm, "end": v(28.13, 4.73) * mm});
            skLineSegment(sketch, "E832", {"start": v(28.13, 4.73) * mm, "end": v(27.22, 6.56) * mm});
            skLineSegment(sketch, "E833", {"start": v(-17.39, 12.35) * mm, "end": v(-13.86, 13.55) * mm});
            skLineSegment(sketch, "E834", {"start": v(-13.86, 13.55) * mm, "end": v(-10.42, 14.47) * mm});
            skLineSegment(sketch, "E835", {"start": v(-28.42, -1.06) * mm, "end": v(-28.53, 0.8) * mm});
            skLineSegment(sketch, "E836", {"start": v(-26.09, 6.1) * mm, "end": v(-24.55, 7.71) * mm});
            skLineSegment(sketch, "E837", {"start": v(-24.55, 7.71) * mm, "end": v(-22.73, 9.21) * mm});
            skLineSegment(sketch, "E838", {"start": v(-7.07, 15.14) * mm, "end": v(-3.81, 15.57) * mm});
            skLineSegment(sketch, "E839", {"start": v(-3.81, 15.57) * mm, "end": v(-0.67, 15.78) * mm});
            skLineSegment(sketch, "E840", {"start": v(-0.67, 15.78) * mm, "end": v(2.36, 15.79) * mm});
            skLineSegment(sketch, "E841", {"start": v(2.36, 15.79) * mm, "end": v(5.26, 15.62) * mm});
            skLineSegment(sketch, "E842", {"start": v(5.26, 15.62) * mm, "end": v(8.03, 15.3) * mm});
            skLineSegment(sketch, "E843", {"start": v(8.03, 15.3) * mm, "end": v(10.65, 14.83) * mm});
            skLineSegment(sketch, "E844", {"start": v(10.65, 14.83) * mm, "end": v(13.11, 14.26) * mm});
            skLineSegment(sketch, "E845", {"start": v(13.11, 14.26) * mm, "end": v(15.41, 13.58) * mm});
            skLineSegment(sketch, "E846", {"start": v(15.41, 13.58) * mm, "end": v(16.48, 13.21) * mm});
            skLineSegment(sketch, "E847", {"start": v(-27.76, -2.95) * mm, "end": v(-28.42, -1.06) * mm});
            skLineSegment(sketch, "E848", {"start": v(-22.73, 9.21) * mm, "end": v(-20.7, 10.59) * mm});
            skLineSegment(sketch, "E849", {"start": v(-20.7, 10.59) * mm, "end": v(-18.53, 11.81) * mm});
            skLineSegment(sketch, "E850", {"start": v(-18.53, 11.81) * mm, "end": v(-17.39, 12.35) * mm});
            skLineSegment(sketch, "E851", {"start": v(7.71, -9.82) * mm, "end": v(12.04, -10.07) * mm});
            skLineSegment(sketch, "E852", {"start": v(12.04, -10.07) * mm, "end": v(13.94, -10) * mm});
            skLineSegment(sketch, "E853", {"start": v(13.94, -10) * mm, "end": v(14.56, -9.98) * mm});
            skLineSegment(sketch, "E854", {"start": v(14.56, -9.98) * mm, "end": v(15.27, -9.95) * mm});
            skLineSegment(sketch, "E855", {"start": v(-28.53, 0.8) * mm, "end": v(-28.14, 2.63) * mm});
            skLineSegment(sketch, "E856", {"start": v(-28.14, 2.63) * mm, "end": v(-27.3, 4.4) * mm});
            skLineSegment(sketch, "E857", {"start": v(-27.3, 4.4) * mm, "end": v(-26.09, 6.1) * mm});
            skLineSegment(sketch, "E858", {"start": v(19.7, -9.2) * mm, "end": v(18.73, -9.44) * mm});
            skLineSegment(sketch, "E859", {"start": v(16.06, -9.88) * mm, "end": v(15.27, -9.95) * mm});
            skLineSegment(sketch, "E860", {"start": v(22.6, -8.12) * mm, "end": v(21.64, -8.54) * mm});
            skLineSegment(sketch, "E861", {"start": v(21.64, -8.54) * mm, "end": v(20.67, -8.9) * mm});
            skLineSegment(sketch, "E862", {"start": v(18.73, -9.44) * mm, "end": v(17.8, -9.63) * mm});
            skLineSegment(sketch, "E863", {"start": v(17.8, -9.63) * mm, "end": v(16.9, -9.78) * mm});
            skLineSegment(sketch, "E864", {"start": v(16.9, -9.78) * mm, "end": v(16.06, -9.88) * mm});
            skLineSegment(sketch, "E865", {"start": v(7.71, -9.82) * mm, "end": v(7.47, -9.82) * mm});
            skLineSegment(sketch, "E866", {"start": v(7.47, -9.82) * mm, "end": v(7.24, -9.82) * mm});
            skLineSegment(sketch, "E867", {"start": v(7.24, -9.82) * mm, "end": v(7.03, -9.81) * mm});
            skLineSegment(sketch, "E868", {"start": v(7.03, -9.81) * mm, "end": v(6.84, -9.8) * mm});
            skLineSegment(sketch, "E869", {"start": v(6.84, -9.8) * mm, "end": v(6.65, -9.8) * mm});
            skLineSegment(sketch, "E870", {"start": v(6.65, -9.8) * mm, "end": v(6.47, -9.78) * mm});
            skLineSegment(sketch, "E871", {"start": v(6.47, -9.78) * mm, "end": v(6.28, -9.75) * mm});
            skLineSegment(sketch, "E872", {"start": v(6.28, -9.75) * mm, "end": v(6.1, -9.72) * mm});
            skLineSegment(sketch, "E873", {"start": v(6.1, -9.72) * mm, "end": v(5.9, -9.68) * mm});
            skLineSegment(sketch, "E874", {"start": v(5.9, -9.68) * mm, "end": v(5.7, -9.62) * mm});
            skLineSegment(sketch, "E875", {"start": v(28.93, 0.92) * mm, "end": v(28.75, -0.45) * mm});
            skLineSegment(sketch, "E876", {"start": v(28.75, -0.45) * mm, "end": v(28.44, -1.7) * mm});
            skLineSegment(sketch, "E877", {"start": v(28.44, -1.7) * mm, "end": v(28, -2.85) * mm});
            skLineSegment(sketch, "E878", {"start": v(28, -2.85) * mm, "end": v(27.46, -3.88) * mm});
            skLineSegment(sketch, "E879", {"start": v(27.46, -3.88) * mm, "end": v(26.82, -4.81) * mm});
            skLineSegment(sketch, "E880", {"start": v(26.82, -4.81) * mm, "end": v(26.1, -5.65) * mm});
            skLineSegment(sketch, "E881", {"start": v(26.1, -5.65) * mm, "end": v(25.3, -6.4) * mm});
            skLineSegment(sketch, "E882", {"start": v(25.3, -6.4) * mm, "end": v(24.45, -7.05) * mm});
            skLineSegment(sketch, "E883", {"start": v(24.45, -7.05) * mm, "end": v(23.54, -7.62) * mm});
            skLineSegment(sketch, "E884", {"start": v(23.54, -7.62) * mm, "end": v(22.6, -8.12) * mm});
            skLineSegment(sketch, "E885", {"start": v(-26.27, -5.37) * mm, "end": v(-26.63, -4.93) * mm});
            skLineSegment(sketch, "E886", {"start": v(-26.63, -4.93) * mm, "end": v(-26.93, -4.51) * mm});
            skLineSegment(sketch, "E887", {"start": v(-26.93, -4.51) * mm, "end": v(-27.18, -4.12) * mm});
            skLineSegment(sketch, "E888", {"start": v(-27.18, -4.12) * mm, "end": v(-27.39, -3.77) * mm});
            skLineSegment(sketch, "E889", {"start": v(-27.39, -3.77) * mm, "end": v(-27.55, -3.45) * mm});
            skLineSegment(sketch, "E890", {"start": v(-27.55, -3.45) * mm, "end": v(-27.67, -3.18) * mm});
            skLineSegment(sketch, "E891", {"start": v(-27.67, -3.18) * mm, "end": v(-27.76, -2.95) * mm});
            skLineSegment(sketch, "E892", {"start": v(-14.1, -12.03) * mm, "end": v(-15.66, -11.55) * mm});
            skLineSegment(sketch, "E893", {"start": v(-15.66, -11.55) * mm, "end": v(-17.09, -11.05) * mm});
            skLineSegment(sketch, "E894", {"start": v(-17.09, -11.05) * mm, "end": v(-18.4, -10.54) * mm});
            skLineSegment(sketch, "E895", {"start": v(-18.4, -10.54) * mm, "end": v(-19.61, -10.01) * mm});
            skLineSegment(sketch, "E896", {"start": v(-19.61, -10.01) * mm, "end": v(-20.71, -9.48) * mm});
            skLineSegment(sketch, "E897", {"start": v(-20.71, -9.48) * mm, "end": v(-21.71, -8.95) * mm});
            skLineSegment(sketch, "E898", {"start": v(-21.71, -8.95) * mm, "end": v(-22.61, -8.4) * mm});
            skLineSegment(sketch, "E899", {"start": v(-22.61, -8.4) * mm, "end": v(-23.42, -7.88) * mm});
            skLineSegment(sketch, "E900", {"start": v(-23.42, -7.88) * mm, "end": v(-24.14, -7.35) * mm});
            skLineSegment(sketch, "E901", {"start": v(-24.14, -7.35) * mm, "end": v(-24.79, -6.83) * mm});
            skLineSegment(sketch, "E902", {"start": v(-24.79, -6.83) * mm, "end": v(-25.35, -6.33) * mm});
            skLineSegment(sketch, "E903", {"start": v(-25.35, -6.33) * mm, "end": v(-25.84, -5.84) * mm});
            skLineSegment(sketch, "E904", {"start": v(-25.84, -5.84) * mm, "end": v(-26.27, -5.37) * mm});
            skLineSegment(sketch, "E905", {"start": v(5.7, -9.62) * mm, "end": v(5.47, -9.56) * mm});
            skLineSegment(sketch, "E906", {"start": v(5.47, -9.56) * mm, "end": v(5.23, -9.48) * mm});
            skLineSegment(sketch, "E907", {"start": v(5.23, -9.48) * mm, "end": v(4.96, -9.4) * mm});
            skLineSegment(sketch, "E908", {"start": v(4.96, -9.4) * mm, "end": v(4.66, -9.29) * mm});
            skLineSegment(sketch, "E909", {"start": v(4.66, -9.29) * mm, "end": v(4.33, -9.17) * mm});
            skLineSegment(sketch, "E910", {"start": v(4.33, -9.17) * mm, "end": v(3.96, -9.03) * mm});
            skLineSegment(sketch, "E911", {"start": v(3.96, -9.03) * mm, "end": v(3.55, -8.87) * mm});
            skLineSegment(sketch, "E912", {"start": v(3.55, -8.87) * mm, "end": v(3.1, -8.7) * mm});
            skLineSegment(sketch, "E913", {"start": v(3.1, -8.7) * mm, "end": v(2.59, -8.5) * mm});
            skLineSegment(sketch, "E914", {"start": v(2.59, -8.5) * mm, "end": v(2.03, -8.28) * mm});
            skLineSegment(sketch, "E915", {"start": v(19.7, -9.2) * mm, "end": v(20.67, -8.9) * mm});
            skLineSegment(sketch, "E916", {"start": v(-2.87, -15.56) * mm, "end": v(-2.2, -14.85) * mm});
            skLineSegment(sketch, "E917", {"start": v(-2.2, -14.85) * mm, "end": v(-1.59, -14.22) * mm});
            skLineSegment(sketch, "E918", {"start": v(-1.59, -14.22) * mm, "end": v(-1, -13.67) * mm});
            skLineSegment(sketch, "E919", {"start": v(-1, -13.67) * mm, "end": v(-0.47, -13.2) * mm});
            skLineSegment(sketch, "E920", {"start": v(-0.47, -13.2) * mm, "end": v(0.04, -12.8) * mm});
            skLineSegment(sketch, "E921", {"start": v(0.04, -12.8) * mm, "end": v(0.52, -12.45) * mm});
            skLineSegment(sketch, "E922", {"start": v(0.52, -12.45) * mm, "end": v(0.97, -12.17) * mm});
            skLineSegment(sketch, "E923", {"start": v(0.97, -12.17) * mm, "end": v(1.4, -11.94) * mm});
            skLineSegment(sketch, "E924", {"start": v(1.4, -11.94) * mm, "end": v(1.8, -11.76) * mm});
            skLineSegment(sketch, "E925", {"start": v(1.8, -11.76) * mm, "end": v(2.17, -11.62) * mm});
            skLineSegment(sketch, "E926", {"start": v(2.17, -11.62) * mm, "end": v(2.54, -11.52) * mm});
            skLineSegment(sketch, "E927", {"start": v(2.54, -11.52) * mm, "end": v(2.89, -11.45) * mm});
            skLineSegment(sketch, "E928", {"start": v(2.89, -11.45) * mm, "end": v(3.23, -11.41) * mm});
            skLineSegment(sketch, "E929", {"start": v(3.23, -11.41) * mm, "end": v(3.56, -11.4) * mm});
            skLineSegment(sketch, "E930", {"start": v(3.56, -11.4) * mm, "end": v(3.88, -11.4) * mm});
            skLineSegment(sketch, "E931", {"start": v(3.88, -11.4) * mm, "end": v(4.2, -11.42) * mm});
            skLineSegment(sketch, "E932", {"start": v(4.2, -11.42) * mm, "end": v(4.52, -11.44) * mm});
            skLineSegment(sketch, "E933", {"start": v(4.52, -11.44) * mm, "end": v(4.85, -11.46) * mm});
            skLineSegment(sketch, "E934", {"start": v(4.85, -11.46) * mm, "end": v(5.18, -11.49) * mm});
            skLineSegment(sketch, "E935", {"start": v(5.86, -11.58) * mm, "end": v(6.17, -11.65) * mm});
            skLineSegment(sketch, "E936", {"start": v(6.17, -11.65) * mm, "end": v(6.45, -11.71) * mm});
            skLineSegment(sketch, "E937", {"start": v(6.45, -11.71) * mm, "end": v(6.7, -11.77) * mm});
            skLineSegment(sketch, "E938", {"start": v(6.7, -11.77) * mm, "end": v(6.94, -11.81) * mm});
            skLineSegment(sketch, "E939", {"start": v(6.94, -11.81) * mm, "end": v(7.15, -11.85) * mm});
            skLineSegment(sketch, "E940", {"start": v(7.15, -11.85) * mm, "end": v(7.34, -11.88) * mm});
            skLineSegment(sketch, "E941", {"start": v(7.34, -11.88) * mm, "end": v(7.53, -11.9) * mm});
            skLineSegment(sketch, "E942", {"start": v(7.53, -11.9) * mm, "end": v(7.7, -11.93) * mm});
            skLineSegment(sketch, "E943", {"start": v(7.7, -11.93) * mm, "end": v(7.86, -11.94) * mm});
            skLineSegment(sketch, "E944", {"start": v(7.86, -11.94) * mm, "end": v(8.02, -11.96) * mm});
            skLineSegment(sketch, "E945", {"start": v(8.02, -11.96) * mm, "end": v(8.18, -11.96) * mm});
            skLineSegment(sketch, "E946", {"start": v(8.18, -11.96) * mm, "end": v(8.34, -11.97) * mm});
            skLineSegment(sketch, "E947", {"start": v(8.34, -11.97) * mm, "end": v(8.51, -11.97) * mm});
            skLineSegment(sketch, "E948", {"start": v(8.51, -11.97) * mm, "end": v(8.69, -11.97) * mm});
            skLineSegment(sketch, "E949", {"start": v(8.69, -11.97) * mm, "end": v(8.87, -11.96) * mm});
            skLineSegment(sketch, "E950", {"start": v(8.87, -11.96) * mm, "end": v(9.07, -11.96) * mm});
            skLineSegment(sketch, "E951", {"start": v(9.07, -11.96) * mm, "end": v(9.3, -11.96) * mm});
            skLineSegment(sketch, "E952", {"start": v(9.3, -11.96) * mm, "end": v(9.53, -11.96) * mm});
            skLineSegment(sketch, "E953", {"start": v(9.53, -11.96) * mm, "end": v(9.8, -11.95) * mm});
            skLineSegment(sketch, "E954", {"start": v(7.02, -12.34) * mm, "end": v(6.04, -12.2) * mm});
            skLineSegment(sketch, "E955", {"start": v(6.04, -12.2) * mm, "end": v(5.14, -12.14) * mm});
            skLineSegment(sketch, "E956", {"start": v(5.14, -12.14) * mm, "end": v(4.32, -12.14) * mm});
            skLineSegment(sketch, "E957", {"start": v(4.32, -12.14) * mm, "end": v(3.56, -12.2) * mm});
            skLineSegment(sketch, "E958", {"start": v(3.56, -12.2) * mm, "end": v(2.88, -12.32) * mm});
            skLineSegment(sketch, "E959", {"start": v(2.88, -12.32) * mm, "end": v(2.26, -12.49) * mm});
            skLineSegment(sketch, "E960", {"start": v(2.26, -12.49) * mm, "end": v(1.7, -12.7) * mm});
            skLineSegment(sketch, "E961", {"start": v(1.7, -12.7) * mm, "end": v(1.2, -12.94) * mm});
            skLineSegment(sketch, "E962", {"start": v(1.2, -12.94) * mm, "end": v(0.76, -13.2) * mm});
            skLineSegment(sketch, "E963", {"start": v(0.76, -13.2) * mm, "end": v(0.38, -13.5) * mm});
            skLineSegment(sketch, "E964", {"start": v(0.38, -13.5) * mm, "end": v(0.04, -13.82) * mm});
            skLineSegment(sketch, "E965", {"start": v(0.04, -13.82) * mm, "end": v(-0.25, -14.15) * mm});
            skLineSegment(sketch, "E966", {"start": v(-0.25, -14.15) * mm, "end": v(-0.49, -14.48) * mm});
            skLineSegment(sketch, "E967", {"start": v(-0.49, -14.48) * mm, "end": v(-0.69, -14.81) * mm});
            skLineSegment(sketch, "E968", {"start": v(-0.69, -14.81) * mm, "end": v(-0.85, -15.14) * mm});
            skLineSegment(sketch, "E969", {"start": v(-0.85, -15.14) * mm, "end": v(-0.98, -15.45) * mm});
            skLineSegment(sketch, "E970", {"start": v(-0.98, -15.45) * mm, "end": v(-1.07, -15.75) * mm});
            skLineSegment(sketch, "E971", {"start": v(-1.07, -15.75) * mm, "end": v(-1.13, -16.02) * mm});
            skLineSegment(sketch, "E972", {"start": v(9.8, -11.95) * mm, "end": v(10.54, -11.95) * mm});
            skLineSegment(sketch, "E973", {"start": v(10.54, -11.95) * mm, "end": v(11.22, -11.95) * mm});
            skLineSegment(sketch, "E974", {"start": v(11.22, -11.95) * mm, "end": v(11.83, -11.95) * mm});
            skLineSegment(sketch, "E975", {"start": v(11.83, -11.95) * mm, "end": v(12.38, -11.95) * mm});
            skLineSegment(sketch, "E976", {"start": v(12.38, -11.95) * mm, "end": v(12.87, -11.95) * mm});
            skLineSegment(sketch, "E977", {"start": v(12.87, -11.95) * mm, "end": v(13.3, -11.95) * mm});
            skLineSegment(sketch, "E978", {"start": v(13.3, -11.95) * mm, "end": v(13.7, -11.94) * mm});
            skLineSegment(sketch, "E979", {"start": v(13.7, -11.94) * mm, "end": v(14.05, -11.94) * mm});
            skLineSegment(sketch, "E980", {"start": v(14.05, -11.94) * mm, "end": v(14.36, -11.93) * mm});
            skLineSegment(sketch, "E981", {"start": v(14.36, -11.93) * mm, "end": v(14.65, -11.92) * mm});
            skLineSegment(sketch, "E982", {"start": v(14.65, -11.92) * mm, "end": v(14.9, -11.9) * mm});
            skLineSegment(sketch, "E983", {"start": v(14.9, -11.9) * mm, "end": v(15.14, -11.9) * mm});
            skLineSegment(sketch, "E984", {"start": v(15.14, -11.9) * mm, "end": v(15.36, -11.88) * mm});
            skLineSegment(sketch, "E985", {"start": v(15.36, -11.88) * mm, "end": v(15.57, -11.86) * mm});
            skLineSegment(sketch, "E986", {"start": v(15.57, -11.86) * mm, "end": v(15.78, -11.83) * mm});
            skLineSegment(sketch, "E987", {"start": v(15.78, -11.83) * mm, "end": v(15.99, -11.8) * mm});
            skLineSegment(sketch, "E988", {"start": v(15.99, -11.8) * mm, "end": v(16.2, -11.78) * mm});
            skLineSegment(sketch, "E989", {"start": v(16.2, -11.78) * mm, "end": v(16.42, -11.75) * mm});
            skLineSegment(sketch, "E990", {"start": v(16.42, -11.75) * mm, "end": v(16.66, -11.7) * mm});
            skLineSegment(sketch, "E991", {"start": v(-25.96, 12.11) * mm, "end": v(-27.96, 10.68) * mm});
            skLineSegment(sketch, "E992", {"start": v(-27.96, 10.68) * mm, "end": v(-29.63, 9.26) * mm});
            skLineSegment(sketch, "E993", {"start": v(-29.63, 9.26) * mm, "end": v(-29.99, 8.9) * mm});
            skLineSegment(sketch, "E994", {"start": v(16.48, 13.21) * mm, "end": v(17.54, 12.84) * mm});
            skLineSegment(sketch, "E995", {"start": v(17.54, 12.84) * mm, "end": v(19.49, 12.03) * mm});
            skLineSegment(sketch, "E996", {"start": v(19.49, 12.03) * mm, "end": v(21.24, 11.2) * mm});
            skLineSegment(sketch, "E997", {"start": v(21.24, 11.2) * mm, "end": v(22.8, 10.34) * mm});
            skLineSegment(sketch, "E998", {"start": v(22.8, 10.34) * mm, "end": v(24.14, 9.49) * mm});
            skLineSegment(sketch, "E999", {"start": v(24.14, 9.49) * mm, "end": v(25.26, 8.67) * mm});
            skLineSegment(sketch, "E1000", {"start": v(25.26, 8.67) * mm, "end": v(26.16, 7.89) * mm});
            skLineSegment(sketch, "E1001", {"start": v(26.16, 7.89) * mm, "end": v(26.81, 7.18) * mm});
            skLineSegment(sketch, "E1002", {"start": v(26.81, 7.18) * mm, "end": v(27.22, 6.56) * mm});
            skLineSegment(sketch, "E1003", {"start": v(18.03, 15.9) * mm, "end": v(17.2, 16.16) * mm});
            skLineSegment(sketch, "E1004", {"start": v(17.2, 16.16) * mm, "end": v(15.65, 16.63) * mm});
            skLineSegment(sketch, "E1005", {"start": v(15.65, 16.63) * mm, "end": v(14.2, 17.02) * mm});
            skLineSegment(sketch, "E1006", {"start": v(14.2, 17.02) * mm, "end": v(12.87, 17.35) * mm});
            skLineSegment(sketch, "E1007", {"start": v(12.87, 17.35) * mm, "end": v(11.71, 17.62) * mm});
            skLineSegment(sketch, "E1008", {"start": v(11.71, 17.62) * mm, "end": v(10.74, 17.83) * mm});
            skLineSegment(sketch, "E1009", {"start": v(16.66, -11.7) * mm, "end": v(16.92, -11.67) * mm});
            skLineSegment(sketch, "E1010", {"start": v(23.93, -10.4) * mm, "end": v(23.45, -10.71) * mm});
            skLineSegment(sketch, "E1011", {"start": v(23.45, -10.71) * mm, "end": v(22.58, -11.19) * mm});
            skLineSegment(sketch, "E1012", {"start": v(22.58, -11.19) * mm, "end": v(21.74, -11.6) * mm});
            skLineSegment(sketch, "E1013", {"start": v(21.74, -11.6) * mm, "end": v(20.93, -11.98) * mm});
            skLineSegment(sketch, "E1014", {"start": v(20.93, -11.98) * mm, "end": v(20.15, -12.3) * mm});
            skLineSegment(sketch, "E1015", {"start": v(20.15, -12.3) * mm, "end": v(19.4, -12.57) * mm});
            skLineSegment(sketch, "E1016", {"start": v(19.4, -12.57) * mm, "end": v(18.67, -12.8) * mm});
            skLineSegment(sketch, "E1017", {"start": v(18.67, -12.8) * mm, "end": v(17.98, -13.01) * mm});
            skLineSegment(sketch, "E1018", {"start": v(17.98, -13.01) * mm, "end": v(17.3, -13.18) * mm});
            skLineSegment(sketch, "E1019", {"start": v(17.3, -13.18) * mm, "end": v(16.66, -13.32) * mm});
            skLineSegment(sketch, "E1020", {"start": v(16.66, -13.32) * mm, "end": v(16.04, -13.44) * mm});
            skLineSegment(sketch, "E1021", {"start": v(16.04, -13.44) * mm, "end": v(15.45, -13.53) * mm});
            skLineSegment(sketch, "E1022", {"start": v(-30.2, -7.34) * mm, "end": v(-29.92, -7.59) * mm});
            skLineSegment(sketch, "E1023", {"start": v(-29.99, 8.9) * mm, "end": v(-31, 7.86) * mm});
            skLineSegment(sketch, "E1024", {"start": v(-31, 7.86) * mm, "end": v(-32.08, 6.47) * mm});
            skLineSegment(sketch, "E1025", {"start": v(-32.08, 6.47) * mm, "end": v(-32.9, 5.1) * mm});
            skLineSegment(sketch, "E1026", {"start": v(-32.9, 5.1) * mm, "end": v(-33.47, 3.78) * mm});
            skLineSegment(sketch, "E1027", {"start": v(-33.47, 3.78) * mm, "end": v(-33.83, 2.49) * mm});
            skLineSegment(sketch, "E1028", {"start": v(16.92, -11.67) * mm, "end": v(16.19, -11.88) * mm});
            skLineSegment(sketch, "E1029", {"start": v(16.19, -11.88) * mm, "end": v(15.5, -12.07) * mm});
            skLineSegment(sketch, "E1030", {"start": v(15.5, -12.07) * mm, "end": v(14.85, -12.22) * mm});
            skLineSegment(sketch, "E1031", {"start": v(14.85, -12.22) * mm, "end": v(14.23, -12.35) * mm});
            skLineSegment(sketch, "E1032", {"start": v(14.23, -12.35) * mm, "end": v(13.65, -12.46) * mm});
            skLineSegment(sketch, "E1033", {"start": v(13.65, -12.46) * mm, "end": v(13.1, -12.55) * mm});
            skLineSegment(sketch, "E1034", {"start": v(13.1, -12.55) * mm, "end": v(12.57, -12.6) * mm});
            skLineSegment(sketch, "E1035", {"start": v(12.57, -12.6) * mm, "end": v(12.07, -12.65) * mm});
            skLineSegment(sketch, "E1036", {"start": v(12.07, -12.65) * mm, "end": v(11.6, -12.68) * mm});
            skLineSegment(sketch, "E1037", {"start": v(11.6, -12.68) * mm, "end": v(11.13, -12.7) * mm});
            skLineSegment(sketch, "E1038", {"start": v(11.13, -12.7) * mm, "end": v(10.69, -12.7) * mm});
            skLineSegment(sketch, "E1039", {"start": v(10.69, -12.7) * mm, "end": v(10.26, -12.68) * mm});
            skLineSegment(sketch, "E1040", {"start": v(10.26, -12.68) * mm, "end": v(9.84, -12.65) * mm});
            skLineSegment(sketch, "E1041", {"start": v(9.84, -12.65) * mm, "end": v(9.44, -12.62) * mm});
            skLineSegment(sketch, "E1042", {"start": v(9.44, -12.62) * mm, "end": v(9.03, -12.58) * mm});
            skLineSegment(sketch, "E1043", {"start": v(9.03, -12.58) * mm, "end": v(8.64, -12.54) * mm});
            skLineSegment(sketch, "E1044", {"start": v(8.64, -12.54) * mm, "end": v(8.24, -12.49) * mm});
            skLineSegment(sketch, "E1045", {"start": v(8.24, -12.49) * mm, "end": v(7.84, -12.44) * mm});
            skLineSegment(sketch, "E1046", {"start": v(7.84, -12.44) * mm, "end": v(7.43, -12.39) * mm});
            skLineSegment(sketch, "E1047", {"start": v(7.43, -12.39) * mm, "end": v(7.02, -12.34) * mm});
            skLineSegment(sketch, "E1048", {"start": v(6.59, -17.1) * mm, "end": v(6.86, -16.79) * mm});
            skLineSegment(sketch, "E1049", {"start": v(6.86, -16.79) * mm, "end": v(7.12, -16.48) * mm});
            skLineSegment(sketch, "E1050", {"start": v(7.12, -16.48) * mm, "end": v(7.39, -16.2) * mm});
            skLineSegment(sketch, "E1051", {"start": v(7.39, -16.2) * mm, "end": v(7.64, -15.94) * mm});
            skLineSegment(sketch, "E1052", {"start": v(7.64, -15.94) * mm, "end": v(7.9, -15.7) * mm});
            skLineSegment(sketch, "E1053", {"start": v(7.9, -15.7) * mm, "end": v(8.13, -15.48) * mm});
            skLineSegment(sketch, "E1054", {"start": v(8.13, -15.48) * mm, "end": v(8.37, -15.27) * mm});
            skLineSegment(sketch, "E1055", {"start": v(8.37, -15.27) * mm, "end": v(8.6, -15.09) * mm});
            skLineSegment(sketch, "E1056", {"start": v(8.6, -15.09) * mm, "end": v(8.8, -14.92) * mm});
            skLineSegment(sketch, "E1057", {"start": v(8.8, -14.92) * mm, "end": v(9, -14.77) * mm});
            skLineSegment(sketch, "E1058", {"start": v(9, -14.77) * mm, "end": v(9.2, -14.63) * mm});
            skLineSegment(sketch, "E1059", {"start": v(9.2, -14.63) * mm, "end": v(9.38, -14.5) * mm});
            skLineSegment(sketch, "E1060", {"start": v(9.38, -14.5) * mm, "end": v(9.54, -14.4) * mm});
            skLineSegment(sketch, "E1061", {"start": v(9.54, -14.4) * mm, "end": v(9.69, -14.31) * mm});
            skLineSegment(sketch, "E1062", {"start": v(9.69, -14.31) * mm, "end": v(9.82, -14.23) * mm});
            skLineSegment(sketch, "E1063", {"start": v(9.82, -14.23) * mm, "end": v(9.94, -14.17) * mm});
            skLineSegment(sketch, "E1064", {"start": v(9.94, -14.17) * mm, "end": v(10.02, -14.11) * mm});
            skLineSegment(sketch, "E1065", {"start": v(10.02, -14.11) * mm, "end": v(10.12, -14.08) * mm});
            skLineSegment(sketch, "E1066", {"start": v(10.12, -14.08) * mm, "end": v(10.18, -14.05) * mm});
            skLineSegment(sketch, "E1067", {"start": v(10.18, -14.05) * mm, "end": v(10.22, -14.03) * mm});
            skLineSegment(sketch, "E1068", {"start": v(10.22, -14.03) * mm, "end": v(10.4, -13.95) * mm});
            skLineSegment(sketch, "E1069", {"start": v(14.8, -13.14) * mm, "end": v(14.6, -13.15) * mm});
            skLineSegment(sketch, "E1070", {"start": v(14.6, -13.15) * mm, "end": v(14.4, -13.16) * mm});
            skLineSegment(sketch, "E1071", {"start": v(14.4, -13.16) * mm, "end": v(14.2, -13.18) * mm});
            skLineSegment(sketch, "E1072", {"start": v(14.2, -13.18) * mm, "end": v(13.57, -13.25) * mm});
            skLineSegment(sketch, "E1073", {"start": v(13.57, -13.25) * mm, "end": v(13, -13.32) * mm});
            skLineSegment(sketch, "E1074", {"start": v(13, -13.32) * mm, "end": v(12.5, -13.4) * mm});
            skLineSegment(sketch, "E1075", {"start": v(12.5, -13.4) * mm, "end": v(12.06, -13.47) * mm});
            skLineSegment(sketch, "E1076", {"start": v(12.06, -13.47) * mm, "end": v(11.66, -13.55) * mm});
            skLineSegment(sketch, "E1077", {"start": v(11.66, -13.55) * mm, "end": v(11.3, -13.64) * mm});
            skLineSegment(sketch, "E1078", {"start": v(11.3, -13.64) * mm, "end": v(10.97, -13.74) * mm});
            skLineSegment(sketch, "E1079", {"start": v(10.97, -13.74) * mm, "end": v(10.68, -13.84) * mm});
            skLineSegment(sketch, "E1080", {"start": v(10.68, -13.84) * mm, "end": v(10.4, -13.95) * mm});
            skLineSegment(sketch, "E1081", {"start": v(16.05, -13) * mm, "end": v(16.13, -12.97) * mm});
            skLineSegment(sketch, "E1082", {"start": v(16.13, -12.97) * mm, "end": v(16.21, -12.95) * mm});
            skLineSegment(sketch, "E1083", {"start": v(16.21, -12.95) * mm, "end": v(16.3, -12.92) * mm});
            skLineSegment(sketch, "E1084", {"start": v(15.45, -13.53) * mm, "end": v(14.48, -13.56) * mm});
            skLineSegment(sketch, "E1085", {"start": v(14.48, -13.56) * mm, "end": v(13.61, -13.62) * mm});
            skLineSegment(sketch, "E1086", {"start": v(13.61, -13.62) * mm, "end": v(12.84, -13.72) * mm});
            skLineSegment(sketch, "E1087", {"start": v(12.84, -13.72) * mm, "end": v(12.15, -13.85) * mm});
            skLineSegment(sketch, "E1088", {"start": v(12.15, -13.85) * mm, "end": v(11.54, -14.01) * mm});
            skLineSegment(sketch, "E1089", {"start": v(11.54, -14.01) * mm, "end": v(11.02, -14.2) * mm});
            skLineSegment(sketch, "E1090", {"start": v(11.02, -14.2) * mm, "end": v(10.57, -14.4) * mm});
            skLineSegment(sketch, "E1091", {"start": v(10.57, -14.4) * mm, "end": v(10.18, -14.63) * mm});
            skLineSegment(sketch, "E1092", {"start": v(10.18, -14.63) * mm, "end": v(9.86, -14.87) * mm});
            skLineSegment(sketch, "E1093", {"start": v(9.86, -14.87) * mm, "end": v(9.6, -15.11) * mm});
            skLineSegment(sketch, "E1094", {"start": v(9.6, -15.11) * mm, "end": v(9.39, -15.36) * mm});
            skLineSegment(sketch, "E1095", {"start": v(9.39, -15.36) * mm, "end": v(9.23, -15.62) * mm});
            skLineSegment(sketch, "E1096", {"start": v(9.23, -15.62) * mm, "end": v(9.11, -15.87) * mm});
            skLineSegment(sketch, "E1097", {"start": v(9.11, -15.87) * mm, "end": v(9.03, -16.11) * mm});
            skLineSegment(sketch, "E1098", {"start": v(9.03, -16.11) * mm, "end": v(8.99, -16.35) * mm});
            skLineSegment(sketch, "E1099", {"start": v(23.51, -10.62) * mm, "end": v(23.08, -10.82) * mm});
            skLineSegment(sketch, "E1100", {"start": v(16.05, -13) * mm, "end": v(15.97, -13) * mm});
            skLineSegment(sketch, "E1101", {"start": v(15.97, -13) * mm, "end": v(15.88, -13.03) * mm});
            skLineSegment(sketch, "E1102", {"start": v(15.88, -13.03) * mm, "end": v(15.8, -13.04) * mm});
            skLineSegment(sketch, "E1103", {"start": v(15.8, -13.04) * mm, "end": v(15.7, -13.06) * mm});
            skLineSegment(sketch, "E1104", {"start": v(18.7, -12.32) * mm, "end": v(18.25, -12.43) * mm});
            skLineSegment(sketch, "E1105", {"start": v(15.61, -13.07) * mm, "end": v(15.7, -13.06) * mm});
            skLineSegment(sketch, "E1106", {"start": v(16.5, -12.87) * mm, "end": v(16.4, -12.9) * mm});
            skLineSegment(sketch, "E1107", {"start": v(16.4, -12.9) * mm, "end": v(16.3, -12.92) * mm});
            skLineSegment(sketch, "E1108", {"start": v(16.95, -12.75) * mm, "end": v(16.74, -12.8) * mm});
            skLineSegment(sketch, "E1109", {"start": v(20.9, -11.67) * mm, "end": v(20.46, -11.82) * mm});
            skLineSegment(sketch, "E1110", {"start": v(23.08, -10.82) * mm, "end": v(22.65, -11.01) * mm});
            skLineSegment(sketch, "E1111", {"start": v(22.22, -11.2) * mm, "end": v(21.78, -11.36) * mm});
            skLineSegment(sketch, "E1112", {"start": v(19.13, -12.2) * mm, "end": v(18.7, -12.32) * mm});
            skLineSegment(sketch, "E1113", {"start": v(15.61, -13.07) * mm, "end": v(15.5, -13.08) * mm});
            skLineSegment(sketch, "E1114", {"start": v(15.5, -13.08) * mm, "end": v(15.4, -13.1) * mm});
            skLineSegment(sketch, "E1115", {"start": v(15.4, -13.1) * mm, "end": v(15.27, -13.1) * mm});
            skLineSegment(sketch, "E1116", {"start": v(15.27, -13.1) * mm, "end": v(15.13, -13.12) * mm});
            skLineSegment(sketch, "E1117", {"start": v(15.13, -13.12) * mm, "end": v(14.97, -13.13) * mm});
            skLineSegment(sketch, "E1118", {"start": v(21.34, -11.52) * mm, "end": v(20.9, -11.67) * mm});
            skLineSegment(sketch, "E1119", {"start": v(23.93, -10.4) * mm, "end": v(23.51, -10.62) * mm});
            skLineSegment(sketch, "E1120", {"start": v(16.5, -12.87) * mm, "end": v(16.61, -12.84) * mm});
            skLineSegment(sketch, "E1121", {"start": v(22.65, -11.01) * mm, "end": v(22.22, -11.2) * mm});
            skLineSegment(sketch, "E1122", {"start": v(18.25, -12.43) * mm, "end": v(17.82, -12.54) * mm});
            skLineSegment(sketch, "E1123", {"start": v(14.8, -13.14) * mm, "end": v(14.97, -13.13) * mm});
            skLineSegment(sketch, "E1124", {"start": v(17.38, -12.65) * mm, "end": v(16.95, -12.75) * mm});
            skLineSegment(sketch, "E1125", {"start": v(19.58, -12.08) * mm, "end": v(19.13, -12.2) * mm});
            skLineSegment(sketch, "E1126", {"start": v(21.78, -11.36) * mm, "end": v(21.34, -11.52) * mm});
            skLineSegment(sketch, "E1127", {"start": v(17.82, -12.54) * mm, "end": v(17.38, -12.65) * mm});
            skLineSegment(sketch, "E1128", {"start": v(20.02, -11.95) * mm, "end": v(19.58, -12.08) * mm});
            skLineSegment(sketch, "E1129", {"start": v(20.46, -11.82) * mm, "end": v(20.02, -11.95) * mm});
            skLineSegment(sketch, "E1130", {"start": v(16.74, -12.8) * mm, "end": v(16.61, -12.84) * mm});
            skLineSegment(sketch, "E1131", {"start": v(25.9, -10.49) * mm, "end": v(27.05, -9.77) * mm});
            skLineSegment(sketch, "E1132", {"start": v(27.05, -9.77) * mm, "end": v(28.08, -9.05) * mm});
            skLineSegment(sketch, "E1133", {"start": v(28.08, -9.05) * mm, "end": v(29.01, -8.34) * mm});
            skLineSegment(sketch, "E1134", {"start": v(29.01, -8.34) * mm, "end": v(29.84, -7.64) * mm});
            skLineSegment(sketch, "E1135", {"start": v(29.84, -7.64) * mm, "end": v(30.56, -6.95) * mm});
            skLineSegment(sketch, "E1136", {"start": v(30.56, -6.95) * mm, "end": v(31.2, -6.28) * mm});
            skLineSegment(sketch, "E1137", {"start": v(31.2, -6.28) * mm, "end": v(31.74, -5.64) * mm});
            skLineSegment(sketch, "E1138", {"start": v(31.74, -5.64) * mm, "end": v(32.21, -5.02) * mm});
            skLineSegment(sketch, "E1139", {"start": v(32.21, -5.02) * mm, "end": v(32.6, -4.45) * mm});
            skLineSegment(sketch, "E1140", {"start": v(32.6, -4.45) * mm, "end": v(32.92, -3.91) * mm});
            skLineSegment(sketch, "E1141", {"start": v(32.92, -3.91) * mm, "end": v(33.18, -3.42) * mm});
            skLineSegment(sketch, "E1142", {"start": v(33.18, -3.42) * mm, "end": v(33.38, -2.99) * mm});
            skLineSegment(sketch, "E1143", {"start": v(33.38, -2.99) * mm, "end": v(33.53, -2.6) * mm});
            skLineSegment(sketch, "E1144", {"start": v(33.53, -2.6) * mm, "end": v(33.63, -2.29) * mm});
            skLineSegment(sketch, "E1145", {"start": v(33.63, -2.29) * mm, "end": v(33.69, -2.04) * mm});
            skLineSegment(sketch, "E1146", {"start": v(13.61, -16.77) * mm, "end": v(13.99, -16.42) * mm});
            skLineSegment(sketch, "E1147", {"start": v(13.99, -16.42) * mm, "end": v(14.33, -16.1) * mm});
            skLineSegment(sketch, "E1148", {"start": v(14.33, -16.1) * mm, "end": v(14.64, -15.82) * mm});
            skLineSegment(sketch, "E1149", {"start": v(14.64, -15.82) * mm, "end": v(14.92, -15.57) * mm});
            skLineSegment(sketch, "E1150", {"start": v(14.92, -15.57) * mm, "end": v(15.17, -15.35) * mm});
            skLineSegment(sketch, "E1151", {"start": v(15.17, -15.35) * mm, "end": v(15.4, -15.15) * mm});
            skLineSegment(sketch, "E1152", {"start": v(15.4, -15.15) * mm, "end": v(15.63, -14.98) * mm});
            skLineSegment(sketch, "E1153", {"start": v(15.63, -14.98) * mm, "end": v(15.83, -14.83) * mm});
            skLineSegment(sketch, "E1154", {"start": v(15.83, -14.83) * mm, "end": v(16.02, -14.7) * mm});
            skLineSegment(sketch, "E1155", {"start": v(16.02, -14.7) * mm, "end": v(16.2, -14.59) * mm});
            skLineSegment(sketch, "E1156", {"start": v(16.2, -14.59) * mm, "end": v(16.38, -14.5) * mm});
            skLineSegment(sketch, "E1157", {"start": v(16.38, -14.5) * mm, "end": v(16.55, -14.4) * mm});
            skLineSegment(sketch, "E1158", {"start": v(16.55, -14.4) * mm, "end": v(16.73, -14.33) * mm});
            skLineSegment(sketch, "E1159", {"start": v(16.73, -14.33) * mm, "end": v(16.9, -14.26) * mm});
            skLineSegment(sketch, "E1160", {"start": v(16.9, -14.26) * mm, "end": v(17.09, -14.2) * mm});
            skLineSegment(sketch, "E1161", {"start": v(17.09, -14.2) * mm, "end": v(17.28, -14.13) * mm});
            skLineSegment(sketch, "E1162", {"start": v(17.28, -14.13) * mm, "end": v(17.5, -14.07) * mm});
            skLineSegment(sketch, "E1163", {"start": v(17.5, -14.07) * mm, "end": v(17.72, -14) * mm});
            skLineSegment(sketch, "E1164", {"start": v(17.72, -14) * mm, "end": v(17.96, -13.93) * mm});
            skLineSegment(sketch, "E1165", {"start": v(17.96, -13.93) * mm, "end": v(18.23, -13.85) * mm});
            skLineSegment(sketch, "E1166", {"start": v(18.23, -13.85) * mm, "end": v(20.04, -13.22) * mm});
            skLineSegment(sketch, "E1167", {"start": v(20.04, -13.22) * mm, "end": v(21.7, -12.57) * mm});
            skLineSegment(sketch, "E1168", {"start": v(21.7, -12.57) * mm, "end": v(23.23, -11.89) * mm});
            skLineSegment(sketch, "E1169", {"start": v(23.23, -11.89) * mm, "end": v(24.63, -11.2) * mm});
            skLineSegment(sketch, "E1170", {"start": v(24.63, -11.2) * mm, "end": v(25.9, -10.49) * mm});
            skLineSegment(sketch, "E1171", {"start": v(8.99, -16.35) * mm, "end": v(9.02, -16.74) * mm});
            skLineSegment(sketch, "E1172", {"start": v(9.02, -16.74) * mm, "end": v(9.1, -17.07) * mm});
            skLineSegment(sketch, "E1173", {"start": v(9.1, -17.07) * mm, "end": v(9.23, -17.34) * mm});
            skLineSegment(sketch, "E1174", {"start": v(9.23, -17.34) * mm, "end": v(9.41, -17.56) * mm});
            skLineSegment(sketch, "E1175", {"start": v(9.41, -17.56) * mm, "end": v(9.63, -17.72) * mm});
            skLineSegment(sketch, "E1176", {"start": v(9.63, -17.72) * mm, "end": v(9.87, -17.83) * mm});
            skLineSegment(sketch, "E1177", {"start": v(9.87, -17.83) * mm, "end": v(10.15, -17.9) * mm});
            skLineSegment(sketch, "E1178", {"start": v(10.15, -17.9) * mm, "end": v(10.44, -17.93) * mm});
            skLineSegment(sketch, "E1179", {"start": v(10.44, -17.93) * mm, "end": v(10.75, -17.92) * mm});
            skLineSegment(sketch, "E1180", {"start": v(10.75, -17.92) * mm, "end": v(11.07, -17.89) * mm});
            skLineSegment(sketch, "E1181", {"start": v(11.07, -17.89) * mm, "end": v(11.4, -17.83) * mm});
            skLineSegment(sketch, "E1182", {"start": v(11.4, -17.83) * mm, "end": v(11.72, -17.74) * mm});
            skLineSegment(sketch, "E1183", {"start": v(11.72, -17.74) * mm, "end": v(12.04, -17.64) * mm});
            skLineSegment(sketch, "E1184", {"start": v(12.04, -17.64) * mm, "end": v(12.35, -17.52) * mm});
            skLineSegment(sketch, "E1185", {"start": v(12.35, -17.52) * mm, "end": v(12.63, -17.4) * mm});
            skLineSegment(sketch, "E1186", {"start": v(12.63, -17.4) * mm, "end": v(12.9, -17.27) * mm});
            skLineSegment(sketch, "E1187", {"start": v(12.9, -17.27) * mm, "end": v(13.14, -17.13) * mm});
            skLineSegment(sketch, "E1188", {"start": v(13.14, -17.13) * mm, "end": v(13.34, -17) * mm});
            skLineSegment(sketch, "E1189", {"start": v(13.34, -17) * mm, "end": v(13.5, -16.88) * mm});
            skLineSegment(sketch, "E1190", {"start": v(13.5, -16.88) * mm, "end": v(13.61, -16.77) * mm});
            skLineSegment(sketch, "E1191", {"start": v(33.69, -2.04) * mm, "end": v(34, -0.03) * mm});
            skLineSegment(sketch, "E1192", {"start": v(34, -0.03) * mm, "end": v(33.99, 1.86) * mm});
            skLineSegment(sketch, "E1193", {"start": v(33.99, 1.86) * mm, "end": v(33.68, 3.6) * mm});
            skLineSegment(sketch, "E1194", {"start": v(33.68, 3.6) * mm, "end": v(33.1, 5.24) * mm});
            skLineSegment(sketch, "E1195", {"start": v(33.1, 5.24) * mm, "end": v(32.28, 6.75) * mm});
            skLineSegment(sketch, "E1196", {"start": v(32.28, 6.75) * mm, "end": v(31.25, 8.14) * mm});
            skLineSegment(sketch, "E1197", {"start": v(31.25, 8.14) * mm, "end": v(30.04, 9.42) * mm});
            skLineSegment(sketch, "E1198", {"start": v(30.04, 9.42) * mm, "end": v(28.67, 10.6) * mm});
            skLineSegment(sketch, "E1199", {"start": v(28.67, 10.6) * mm, "end": v(27.18, 11.67) * mm});
            skLineSegment(sketch, "E1200", {"start": v(27.18, 11.67) * mm, "end": v(25.59, 12.64) * mm});
            skLineSegment(sketch, "E1201", {"start": v(25.59, 12.64) * mm, "end": v(23.93, 13.52) * mm});
            skLineSegment(sketch, "E1202", {"start": v(23.93, 13.52) * mm, "end": v(22.24, 14.3) * mm});
            skLineSegment(sketch, "E1203", {"start": v(22.24, 14.3) * mm, "end": v(20.53, 15) * mm});
            skLineSegment(sketch, "E1204", {"start": v(20.53, 15) * mm, "end": v(18.84, 15.63) * mm});
            skLineSegment(sketch, "E1205", {"start": v(18.84, 15.63) * mm, "end": v(18.03, 15.9) * mm});
            skLineSegment(sketch, "E1206", {"start": v(-12.58, 17.26) * mm, "end": v(-14.3, 16.85) * mm});
            skLineSegment(sketch, "E1207", {"start": v(-14.3, 16.85) * mm, "end": v(-15.88, 16.42) * mm});
            skLineSegment(sketch, "E1208", {"start": v(-15.88, 16.42) * mm, "end": v(-17.33, 15.99) * mm});
            skLineSegment(sketch, "E1209", {"start": v(-17.33, 15.99) * mm, "end": v(-18.65, 15.55) * mm});
            skLineSegment(sketch, "E1210", {"start": v(-18.65, 15.55) * mm, "end": v(-19.84, 15.12) * mm});
            skLineSegment(sketch, "E1211", {"start": v(-19.84, 15.12) * mm, "end": v(-20.88, 14.72) * mm});
            skLineSegment(sketch, "E1212", {"start": v(-20.88, 14.72) * mm, "end": v(-21.79, 14.35) * mm});
            skLineSegment(sketch, "E1213", {"start": v(-21.79, 14.35) * mm, "end": v(-22.55, 14.02) * mm});
            skLineSegment(sketch, "E1214", {"start": v(-22.55, 14.02) * mm, "end": v(-23.15, 13.75) * mm});
            skLineSegment(sketch, "E1215", {"start": v(-23.15, 13.75) * mm, "end": v(-23.6, 13.55) * mm});
            skLineSegment(sketch, "E1216", {"start": v(10.74, 17.83) * mm, "end": v(7.95, 18.22) * mm});
            skLineSegment(sketch, "E1217", {"start": v(7.95, 18.22) * mm, "end": v(5.25, 18.49) * mm});
            skLineSegment(sketch, "E1218", {"start": v(5.25, 18.49) * mm, "end": v(2.65, 18.63) * mm});
            skLineSegment(sketch, "E1219", {"start": v(2.65, 18.63) * mm, "end": v(0.15, 18.67) * mm});
            skLineSegment(sketch, "E1220", {"start": v(0.15, 18.67) * mm, "end": v(-2.25, 18.61) * mm});
            skLineSegment(sketch, "E1221", {"start": v(-2.25, 18.61) * mm, "end": v(-4.54, 18.47) * mm});
            skLineSegment(sketch, "E1222", {"start": v(-4.54, 18.47) * mm, "end": v(-6.73, 18.25) * mm});
            skLineSegment(sketch, "E1223", {"start": v(-6.73, 18.25) * mm, "end": v(-8.8, 17.97) * mm});
            skLineSegment(sketch, "E1224", {"start": v(-8.8, 17.97) * mm, "end": v(-10.75, 17.64) * mm});
            skLineSegment(sketch, "E1225", {"start": v(-10.75, 17.64) * mm, "end": v(-12.58, 17.26) * mm});
            skLineSegment(sketch, "E1226", {"start": v(-33.83, 2.49) * mm, "end": v(-34, 1.24) * mm});
            skLineSegment(sketch, "E1227", {"start": v(-34, 1.24) * mm, "end": v(-34, 0.04) * mm});
            skLineSegment(sketch, "E1228", {"start": v(-34, 0.04) * mm, "end": v(-33.84, -1.1) * mm});
            skLineSegment(sketch, "E1229", {"start": v(-33.84, -1.1) * mm, "end": v(-33.56, -2.18) * mm});
            skLineSegment(sketch, "E1230", {"start": v(-33.56, -2.18) * mm, "end": v(-33.18, -3.2) * mm});
            skLineSegment(sketch, "E1231", {"start": v(-33.18, -3.2) * mm, "end": v(-32.7, -4.14) * mm});
            skLineSegment(sketch, "E1232", {"start": v(-32.7, -4.14) * mm, "end": v(-32.18, -5.01) * mm});
            skLineSegment(sketch, "E1233", {"start": v(-32.18, -5.01) * mm, "end": v(-31.62, -5.8) * mm});
            skLineSegment(sketch, "E1234", {"start": v(-31.62, -5.8) * mm, "end": v(-31.04, -6.49) * mm});
            skLineSegment(sketch, "E1235", {"start": v(-31.04, -6.49) * mm, "end": v(-30.47, -7.09) * mm});
            skLineSegment(sketch, "E1236", {"start": v(-30.47, -7.09) * mm, "end": v(-30.2, -7.34) * mm});
            skLineSegment(sketch, "E1237", {"start": v(-24.78, 12.83) * mm, "end": v(-25.96, 12.11) * mm});
            skLineSegment(sketch, "E1238", {"start": v(-23.6, 13.55) * mm, "end": v(-24.78, 12.83) * mm});
            skLineSegment(sketch, "E1239", {"start": v(-23.96, -11.79) * mm, "end": v(-22.96, -12.3) * mm});
            skLineSegment(sketch, "E1240", {"start": v(-22.96, -12.3) * mm, "end": v(-21.97, -12.77) * mm});
            skLineSegment(sketch, "E1241", {"start": v(-21.97, -12.77) * mm, "end": v(-21.01, -13.19) * mm});
            skLineSegment(sketch, "E1242", {"start": v(-21.01, -13.19) * mm, "end": v(-20.08, -13.56) * mm});
            skLineSegment(sketch, "E1243", {"start": v(-20.08, -13.56) * mm, "end": v(-19.18, -13.9) * mm});
            skLineSegment(sketch, "E1244", {"start": v(-19.18, -13.9) * mm, "end": v(-18.31, -14.18) * mm});
            skLineSegment(sketch, "E1245", {"start": v(-18.31, -14.18) * mm, "end": v(-17.5, -14.43) * mm});
            skLineSegment(sketch, "E1246", {"start": v(-17.5, -14.43) * mm, "end": v(-16.73, -14.64) * mm});
            skLineSegment(sketch, "E1247", {"start": v(-16.73, -14.64) * mm, "end": v(-16.03, -14.81) * mm});
            skLineSegment(sketch, "E1248", {"start": v(-16.03, -14.81) * mm, "end": v(-15.39, -14.95) * mm});
            skLineSegment(sketch, "E1249", {"start": v(-15.39, -14.95) * mm, "end": v(-14.82, -15.06) * mm});
            skLineSegment(sketch, "E1250", {"start": v(-14.82, -15.06) * mm, "end": v(-14.33, -15.13) * mm});
            skLineSegment(sketch, "E1251", {"start": v(-14.33, -15.13) * mm, "end": v(-13.92, -15.17) * mm});
            skLineSegment(sketch, "E1252", {"start": v(-13.92, -15.17) * mm, "end": v(-13.6, -15.18) * mm});
            skLineSegment(sketch, "E1253", {"start": v(-29.92, -7.59) * mm, "end": v(-28.96, -8.43) * mm});
            skLineSegment(sketch, "E1254", {"start": v(-28.96, -8.43) * mm, "end": v(-27.98, -9.2) * mm});
            skLineSegment(sketch, "E1255", {"start": v(-27.98, -9.2) * mm, "end": v(-26.98, -9.93) * mm});
            skLineSegment(sketch, "E1256", {"start": v(-26.98, -9.93) * mm, "end": v(-25.98, -10.6) * mm});
            skLineSegment(sketch, "E1257", {"start": v(-25.98, -10.6) * mm, "end": v(-24.97, -11.22) * mm});
            skLineSegment(sketch, "E1258", {"start": v(-24.97, -11.22) * mm, "end": v(-23.96, -11.79) * mm});
            skLineSegment(sketch, "E1259", {"start": v(2.03, -8.28) * mm, "end": v(0.65, -7.6) * mm});
            skLineSegment(sketch, "E1260", {"start": v(0.65, -7.6) * mm, "end": v(-0.7, -7.07) * mm});
            skLineSegment(sketch, "E1261", {"start": v(-0.7, -7.07) * mm, "end": v(-1.98, -6.71) * mm});
            skLineSegment(sketch, "E1262", {"start": v(-1.98, -6.71) * mm, "end": v(-3.22, -6.5) * mm});
            skLineSegment(sketch, "E1263", {"start": v(-3.22, -6.5) * mm, "end": v(-4.4, -6.41) * mm});
            skLineSegment(sketch, "E1264", {"start": v(-4.4, -6.41) * mm, "end": v(-5.53, -6.45) * mm});
            skLineSegment(sketch, "E1265", {"start": v(-5.53, -6.45) * mm, "end": v(-6.59, -6.59) * mm});
            skLineSegment(sketch, "E1266", {"start": v(-6.59, -6.59) * mm, "end": v(-7.59, -6.83) * mm});
            skLineSegment(sketch, "E1267", {"start": v(-7.59, -6.83) * mm, "end": v(-8.52, -7.15) * mm});
            skLineSegment(sketch, "E1268", {"start": v(-8.52, -7.15) * mm, "end": v(-9.37, -7.55) * mm});
            skLineSegment(sketch, "E1269", {"start": v(-9.37, -7.55) * mm, "end": v(-10.15, -8) * mm});
            skLineSegment(sketch, "E1270", {"start": v(-10.15, -8) * mm, "end": v(-10.85, -8.5) * mm});
            skLineSegment(sketch, "E1271", {"start": v(-10.85, -8.5) * mm, "end": v(-11.46, -9.04) * mm});
            skLineSegment(sketch, "E1272", {"start": v(-11.46, -9.04) * mm, "end": v(-11.99, -9.6) * mm});
            skLineSegment(sketch, "E1273", {"start": v(-11.99, -9.6) * mm, "end": v(-12.42, -10.16) * mm});
            skLineSegment(sketch, "E1274", {"start": v(-12.42, -10.16) * mm, "end": v(-12.76, -10.73) * mm});
            skLineSegment(sketch, "E1275", {"start": v(-12.76, -10.73) * mm, "end": v(-13, -11.28) * mm});
            skLineSegment(sketch, "E1276", {"start": v(-13, -11.28) * mm, "end": v(-13.15, -11.8) * mm});
            skLineSegment(sketch, "E1277", {"start": v(-13.15, -11.8) * mm, "end": v(-13.18, -12.3) * mm});
            skLineSegment(sketch, "E1278", {"start": v(-13.18, -12.3) * mm, "end": v(-13.17, -12.32) * mm});
            skLineSegment(sketch, "E1279", {"start": v(-13.17, -12.32) * mm, "end": v(-13.1, -12.73) * mm});
            skLineSegment(sketch, "E1280", {"start": v(-13.1, -12.73) * mm, "end": v(-12.92, -13.55) * mm});
            skLineSegment(sketch, "E1281", {"start": v(-12.92, -13.55) * mm, "end": v(-12.65, -14.26) * mm});
            skLineSegment(sketch, "E1282", {"start": v(-12.65, -14.26) * mm, "end": v(-12.3, -14.86) * mm});
            skLineSegment(sketch, "E1283", {"start": v(-12.3, -14.86) * mm, "end": v(-11.89, -15.37) * mm});
            skLineSegment(sketch, "E1284", {"start": v(-11.89, -15.37) * mm, "end": v(-11.42, -15.8) * mm});
            skLineSegment(sketch, "E1285", {"start": v(-11.42, -15.8) * mm, "end": v(-10.9, -16.13) * mm});
            skLineSegment(sketch, "E1286", {"start": v(-10.9, -16.13) * mm, "end": v(-10.33, -16.4) * mm});
            skLineSegment(sketch, "E1287", {"start": v(-10.33, -16.4) * mm, "end": v(-9.73, -16.58) * mm});
            skLineSegment(sketch, "E1288", {"start": v(-9.73, -16.58) * mm, "end": v(-9.1, -16.7) * mm});
            skLineSegment(sketch, "E1289", {"start": v(-9.1, -16.7) * mm, "end": v(-8.46, -16.77) * mm});
            skLineSegment(sketch, "E1290", {"start": v(-8.46, -16.77) * mm, "end": v(-7.81, -16.78) * mm});
            skLineSegment(sketch, "E1291", {"start": v(-7.81, -16.78) * mm, "end": v(-7.16, -16.75) * mm});
            skLineSegment(sketch, "E1292", {"start": v(-7.16, -16.75) * mm, "end": v(-6.51, -16.68) * mm});
            skLineSegment(sketch, "E1293", {"start": v(-6.51, -16.68) * mm, "end": v(-5.88, -16.57) * mm});
            skLineSegment(sketch, "E1294", {"start": v(-5.88, -16.57) * mm, "end": v(-5.27, -16.44) * mm});
            skLineSegment(sketch, "E1295", {"start": v(-5.27, -16.44) * mm, "end": v(-4.7, -16.28) * mm});
            skLineSegment(sketch, "E1296", {"start": v(-4.7, -16.28) * mm, "end": v(-4.16, -16.1) * mm});
            skLineSegment(sketch, "E1297", {"start": v(-4.16, -16.1) * mm, "end": v(-3.67, -15.93) * mm});
            skLineSegment(sketch, "E1298", {"start": v(-3.67, -15.93) * mm, "end": v(-3.24, -15.74) * mm});
            skLineSegment(sketch, "E1299", {"start": v(-3.24, -15.74) * mm, "end": v(-2.87, -15.56) * mm});
            skLineSegment(sketch, "E1300", {"start": v(-1.13, -16.02) * mm, "end": v(-1.1, -16.42) * mm});
            skLineSegment(sketch, "E1301", {"start": v(-1.1, -16.42) * mm, "end": v(-1.05, -16.79) * mm});
            skLineSegment(sketch, "E1302", {"start": v(-1.05, -16.79) * mm, "end": v(-0.95, -17.11) * mm});
            skLineSegment(sketch, "E1303", {"start": v(-0.95, -17.11) * mm, "end": v(-0.82, -17.4) * mm});
            skLineSegment(sketch, "E1304", {"start": v(-0.82, -17.4) * mm, "end": v(-0.65, -17.65) * mm});
            skLineSegment(sketch, "E1305", {"start": v(-0.65, -17.65) * mm, "end": v(-0.47, -17.86) * mm});
            skLineSegment(sketch, "E1306", {"start": v(-0.47, -17.86) * mm, "end": v(-0.26, -18.05) * mm});
            skLineSegment(sketch, "E1307", {"start": v(-0.26, -18.05) * mm, "end": v(-0.03, -18.2) * mm});
            skLineSegment(sketch, "E1308", {"start": v(-0.03, -18.2) * mm, "end": v(0.22, -18.32) * mm});
            skLineSegment(sketch, "E1309", {"start": v(0.57, -18.44) * mm, "end": v(0.74, -18.49) * mm});
            skLineSegment(sketch, "E1310", {"start": v(0.74, -18.49) * mm, "end": v(0.92, -18.53) * mm});
            skLineSegment(sketch, "E1311", {"start": v(0.22, -18.32) * mm, "end": v(0.47, -18.42) * mm});
            skLineSegment(sketch, "E1312", {"start": v(0.47, -18.42) * mm, "end": v(0.57, -18.44) * mm});
            skLineSegment(sketch, "E1313", {"start": v(2.26, -18.67) * mm, "end": v(2.57, -18.66) * mm});
            skLineSegment(sketch, "E1314", {"start": v(4.7, -18.17) * mm, "end": v(4.9, -18.07) * mm});
            skLineSegment(sketch, "E1315", {"start": v(5.41, -17.84) * mm, "end": v(5.38, -17.87) * mm});
            skLineSegment(sketch, "E1316", {"start": v(5.38, -17.87) * mm, "end": v(5.26, -17.91) * mm});
            skLineSegment(sketch, "E1317", {"start": v(5.09, -18) * mm, "end": v(5.26, -17.91) * mm});
            skLineSegment(sketch, "E1318", {"start": v(0.92, -18.53) * mm, "end": v(1.27, -18.6) * mm});
            skLineSegment(sketch, "E1319", {"start": v(1.27, -18.6) * mm, "end": v(1.6, -18.65) * mm});
            skLineSegment(sketch, "E1320", {"start": v(1.6, -18.65) * mm, "end": v(1.94, -18.67) * mm});
            skLineSegment(sketch, "E1321", {"start": v(1.94, -18.67) * mm, "end": v(2.26, -18.67) * mm});
            skLineSegment(sketch, "E1322", {"start": v(4.9, -18.07) * mm, "end": v(5.09, -18) * mm});
            skLineSegment(sketch, "E1323", {"start": v(2.57, -18.66) * mm, "end": v(2.88, -18.63) * mm});
            skLineSegment(sketch, "E1324", {"start": v(2.88, -18.63) * mm, "end": v(3.17, -18.59) * mm});
            skLineSegment(sketch, "E1325", {"start": v(3.17, -18.59) * mm, "end": v(3.46, -18.53) * mm});
            skLineSegment(sketch, "E1326", {"start": v(3.46, -18.53) * mm, "end": v(3.73, -18.47) * mm});
            skLineSegment(sketch, "E1327", {"start": v(3.73, -18.47) * mm, "end": v(4, -18.4) * mm});
            skLineSegment(sketch, "E1328", {"start": v(4, -18.4) * mm, "end": v(4.24, -18.32) * mm});
            skLineSegment(sketch, "E1329", {"start": v(4.24, -18.32) * mm, "end": v(4.47, -18.24) * mm});
            skLineSegment(sketch, "E1330", {"start": v(4.47, -18.24) * mm, "end": v(4.7, -18.17) * mm});
            skLineSegment(sketch, "E1331", {"start": v(6.59, -17.1) * mm, "end": v(6.42, -17.24) * mm});
            skLineSegment(sketch, "E1332", {"start": v(6.42, -17.24) * mm, "end": v(6.24, -17.36) * mm});
            skLineSegment(sketch, "E1333", {"start": v(6.24, -17.36) * mm, "end": v(6.07, -17.48) * mm});
            skLineSegment(sketch, "E1334", {"start": v(6.07, -17.48) * mm, "end": v(5.9, -17.59) * mm});
            skLineSegment(sketch, "E1335", {"start": v(5.9, -17.59) * mm, "end": v(5.72, -17.69) * mm});
            skLineSegment(sketch, "E1336", {"start": v(5.72, -17.69) * mm, "end": v(5.55, -17.78) * mm});
            skLineSegment(sketch, "E1337", {"start": v(5.55, -17.78) * mm, "end": v(5.41, -17.84) * mm});
            skLineSegment(sketch, "E1338", {"start": v(24.35, -10.17) * mm, "end": v(23.93, -10.4) * mm});
            skLineSegment(sketch, "E1339", {"start": v(5.18, -11.49) * mm, "end": v(5.86, -11.58) * mm});
            skSolve(sketch);
        }
        {
            var Q0;
            Q0 = qSketchRegion(id + "F2", true);
            extrude(context, id + "F3", {"entities" : qUnion([Q0]), "operationType" : NewBodyOperationType.ADD, "endBound" : BoundingType.SYMMETRIC, "depth" : 30 * mm});
        }
        {
            var Q0;
            Q0=qCreatedBy(makeId("Top.planeOp"),FACE);
            var sketch = newSketch(context, id + "F4", { "sketchPlane" : qUnion([Q0])});
            skCircle(sketch, "E1340", {"center": v(0, 45) * mm, "radius": 45 * mm});
            skCircle(sketch, "E1341", {"center": v(0, 43.5) * mm, "radius": 48 * mm});
            skSolve(sketch);
        }
        {
            var Q0;
            Q0 = qSketchRegion(id + "F4", true);
            extrude(context, id + "F5", {"entities" : qUnion([Q0]), "operationType" : NewBodyOperationType.INTERSECT, "endBound" : BoundingType.SYMMETRIC, "depth" : 100 * mm});
        }
    });
